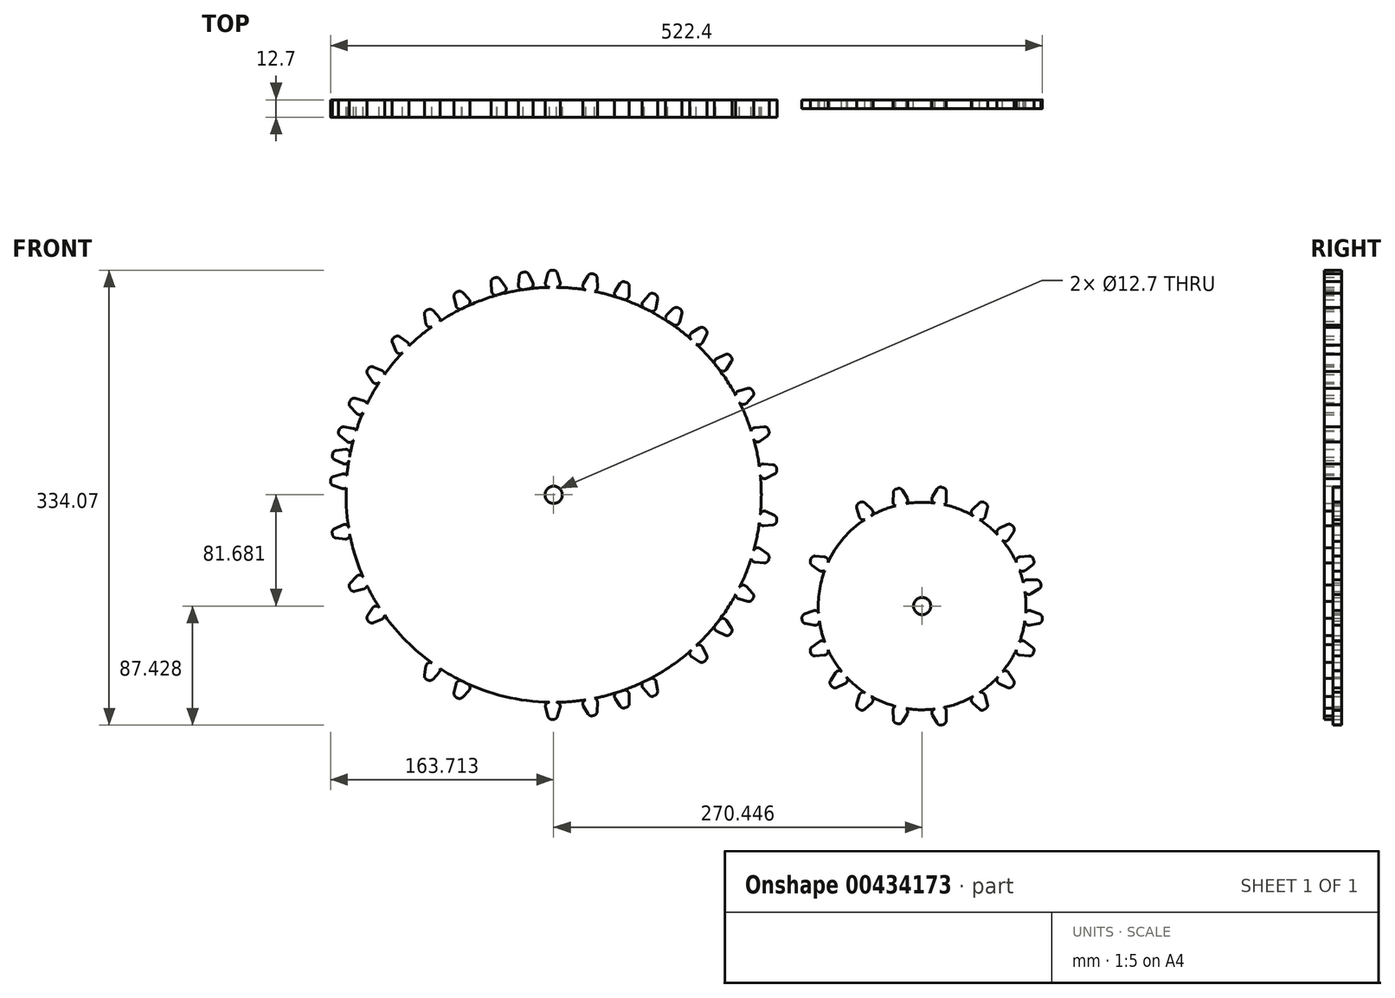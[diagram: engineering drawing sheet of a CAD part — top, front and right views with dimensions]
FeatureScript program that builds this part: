
annotation { "Feature Type Name" : "Feature", "Feature Type Description" : "" }
export const myFeature = defineFeature(function(context is Context, id is Id, definition is map)
    precondition{}
    {
        {
            var Q0;
            Q0=qCreatedBy(makeId("Front.planeOp"),FACE);
            var sketch = newSketch(context, id + "F0", { "sketchPlane" : qUnion([Q0])});
            skCircle(sketch, "E0", {"center": v(-67.8, 42.77) * mm, "radius": 152.4 * mm});
            skCircle(sketch, "E1", {"center": v(227.03, 42.77) * mm, "radius": 76.2 * mm});
            skCircle(sketch, "E2", {"center": v(-67.8, 42.77) * mm, "radius": 6.35 * mm});
            skCircle(sketch, "E3", {"center": v(227.03, 42.77) * mm, "radius": 6.35 * mm});
            skPoint(sketch, "E4.MirrorP", {"position": v(-81.74, -109.18) * mm});
            skLineSegment(sketch, "E5", {"start": v(-69.07, 207.73) * mm, "end": v(-67.96, 207.73) * mm});
            skLineSegment(sketch, "E6", {"start": v(-65.03, 205.55) * mm, "end": v(-63.1, 199.05) * mm});
            skLineSegment(sketch, "E7", {"start": v(-72, 205.48) * mm, "end": v(-73.77, 198.99) * mm});
            skLineSegment(sketch, "E8", {"start": v(-70.83, 195.14) * mm, "end": v(-66.03, 195.14) * mm});
            skArc(sketch, "E9.filletArc", {"start": v(-65.03, 205.55) * mm, "mid": v(-66.13, 207.13) * mm, "end": v(-67.96, 207.73) * mm});
            skArc(sketch, "E10.filletArc", {"start": v(-69.07, 207.73) * mm, "mid": v(-70.92, 207.1) * mm, "end": v(-72, 205.48) * mm});
            skArc(sketch, "E11.filletArc", {"start": v(-66.03, 195.14) * mm, "mid": v(-63.59, 196.36) * mm, "end": v(-63.1, 199.05) * mm});
            skArc(sketch, "E12.filletArc", {"start": v(-73.77, 198.99) * mm, "mid": v(-73.26, 196.34) * mm, "end": v(-70.83, 195.14) * mm});
            skLineSegment(sketch, "E13", {"start": v(-39.2, 205.03) * mm, "end": v(-38.14, 204.74) * mm});
            skLineSegment(sketch, "E14", {"start": v(-35.88, 201.88) * mm, "end": v(-35.7, 195.1) * mm});
            skLineSegment(sketch, "E15", {"start": v(-42.63, 203.62) * mm, "end": v(-46.02, 197.8) * mm});
            skLineSegment(sketch, "E16", {"start": v(-44.17, 193.33) * mm, "end": v(-39.53, 192.08) * mm});
            skArc(sketch, "E17.filletArc", {"start": v(-35.88, 201.88) * mm, "mid": v(-36.53, 203.69) * mm, "end": v(-38.14, 204.74) * mm});
            skArc(sketch, "E18.filletArc", {"start": v(-39.2, 205.03) * mm, "mid": v(-41.16, 204.9) * mm, "end": v(-42.63, 203.62) * mm});
            skArc(sketch, "E19.filletArc", {"start": v(-39.53, 192.08) * mm, "mid": v(-36.86, 192.63) * mm, "end": v(-35.7, 195.1) * mm});
            skArc(sketch, "E20.filletArc", {"start": v(-46.02, 197.8) * mm, "mid": v(-46.2, 195.1) * mm, "end": v(-44.17, 193.33) * mm});
            skLineSegment(sketch, "E21", {"start": v(-111.8, 201.9) * mm, "end": v(-110.75, 202.27) * mm});
            skLineSegment(sketch, "E22", {"start": v(-107.26, 201.22) * mm, "end": v(-103.23, 195.78) * mm});
            skLineSegment(sketch, "E23", {"start": v(-113.8, 198.77) * mm, "end": v(-113.23, 192.07) * mm});
            skLineSegment(sketch, "E24", {"start": v(-109.15, 189.45) * mm, "end": v(-104.64, 191.1) * mm});
            skArc(sketch, "E25.filletArc", {"start": v(-107.26, 201.22) * mm, "mid": v(-108.83, 202.33) * mm, "end": v(-110.75, 202.27) * mm});
            skArc(sketch, "E26.filletArc", {"start": v(-111.8, 201.9) * mm, "mid": v(-113.32, 200.67) * mm, "end": v(-113.8, 198.77) * mm});
            skArc(sketch, "E27.filletArc", {"start": v(-104.64, 191.1) * mm, "mid": v(-102.76, 193.08) * mm, "end": v(-103.23, 195.78) * mm});
            skArc(sketch, "E28.filletArc", {"start": v(-113.23, 192.07) * mm, "mid": v(-111.84, 189.75) * mm, "end": v(-109.15, 189.45) * mm});
            skLineSegment(sketch, "E29", {"start": v(-15.51, 199.28) * mm, "end": v(-14.46, 198.94) * mm});
            skLineSegment(sketch, "E30", {"start": v(-12.33, 195.98) * mm, "end": v(-12.45, 189.2) * mm});
            skLineSegment(sketch, "E31", {"start": v(-19, 198.02) * mm, "end": v(-22.64, 192.36) * mm});
            skLineSegment(sketch, "E32", {"start": v(-21, 187.8) * mm, "end": v(-16.42, 186.35) * mm});
            skArc(sketch, "E33.filletArc", {"start": v(-12.33, 195.98) * mm, "mid": v(-12.9, 197.81) * mm, "end": v(-14.46, 198.94) * mm});
            skArc(sketch, "E34.filletArc", {"start": v(-15.51, 199.28) * mm, "mid": v(-17.47, 199.24) * mm, "end": v(-19, 198.02) * mm});
            skArc(sketch, "E35.filletArc", {"start": v(-16.42, 186.35) * mm, "mid": v(-13.72, 186.78) * mm, "end": v(-12.45, 189.2) * mm});
            skArc(sketch, "E36.filletArc", {"start": v(-22.64, 192.36) * mm, "mid": v(-22.95, 189.68) * mm, "end": v(-21, 187.8) * mm});
            skLineSegment(sketch, "E37", {"start": v(-139.27, 191.52) * mm, "end": v(-138.28, 192.02) * mm});
            skLineSegment(sketch, "E38", {"start": v(-134.69, 191.4) * mm, "end": v(-130.02, 186.5) * mm});
            skLineSegment(sketch, "E39", {"start": v(-140.87, 188.18) * mm, "end": v(-139.49, 181.59) * mm});
            skLineSegment(sketch, "E40", {"start": v(-135.12, 179.5) * mm, "end": v(-130.84, 181.68) * mm});
            skArc(sketch, "E41.filletArc", {"start": v(-134.69, 191.4) * mm, "mid": v(-136.38, 192.31) * mm, "end": v(-138.28, 192.02) * mm});
            skArc(sketch, "E42.filletArc", {"start": v(-139.27, 191.52) * mm, "mid": v(-140.64, 190.12) * mm, "end": v(-140.87, 188.18) * mm});
            skArc(sketch, "E43.filletArc", {"start": v(-130.84, 181.68) * mm, "mid": v(-129.22, 183.88) * mm, "end": v(-130.02, 186.5) * mm});
            skArc(sketch, "E44.filletArc", {"start": v(-139.49, 181.59) * mm, "mid": v(-137.82, 179.46) * mm, "end": v(-135.12, 179.5) * mm});
            skLineSegment(sketch, "E45", {"start": v(5.65, 190.54) * mm, "end": v(6.66, 190.07) * mm});
            skLineSegment(sketch, "E46", {"start": v(8.39, 186.86) * mm, "end": v(7.39, 180.16) * mm});
            skLineSegment(sketch, "E47", {"start": v(2.04, 189.75) * mm, "end": v(-2.3, 184.6) * mm});
            skLineSegment(sketch, "E48", {"start": v(-1.27, 179.88) * mm, "end": v(3.08, 177.85) * mm});
            skArc(sketch, "E49.filletArc", {"start": v(8.39, 186.86) * mm, "mid": v(8.06, 188.75) * mm, "end": v(6.66, 190.07) * mm});
            skArc(sketch, "E50.filletArc", {"start": v(5.65, 190.54) * mm, "mid": v(3.71, 190.76) * mm, "end": v(2.04, 189.75) * mm});
            skArc(sketch, "E51.filletArc", {"start": v(3.08, 177.85) * mm, "mid": v(5.82, 177.93) * mm, "end": v(7.39, 180.16) * mm});
            skArc(sketch, "E52.filletArc", {"start": v(-2.3, 184.6) * mm, "mid": v(-2.96, 181.99) * mm, "end": v(-1.27, 179.88) * mm});
            skLineSegment(sketch, "E53", {"start": v(-90.54, 206.24) * mm, "end": v(-89.44, 206.43) * mm});
            skLineSegment(sketch, "E54", {"start": v(-86.19, 204.8) * mm, "end": v(-83.16, 198.73) * mm});
            skLineSegment(sketch, "E55", {"start": v(-93.04, 203.52) * mm, "end": v(-93.65, 196.81) * mm});
            skLineSegment(sketch, "E56", {"start": v(-90.09, 193.53) * mm, "end": v(-85.36, 194.37) * mm});
            skArc(sketch, "E57.filletArc", {"start": v(-86.19, 204.8) * mm, "mid": v(-87.54, 206.15) * mm, "end": v(-89.44, 206.43) * mm});
            skArc(sketch, "E58.filletArc", {"start": v(-90.54, 206.24) * mm, "mid": v(-92.25, 205.3) * mm, "end": v(-93.04, 203.52) * mm});
            skArc(sketch, "E59.filletArc", {"start": v(-85.36, 194.37) * mm, "mid": v(-83.17, 196) * mm, "end": v(-83.16, 198.73) * mm});
            skArc(sketch, "E60.filletArc", {"start": v(-93.65, 196.81) * mm, "mid": v(-92.68, 194.3) * mm, "end": v(-90.09, 193.53) * mm});
            skLineSegment(sketch, "E61", {"start": v(23.77, 180.12) * mm, "end": v(24.73, 179.56) * mm});
            skLineSegment(sketch, "E62", {"start": v(26.17, 176.21) * mm, "end": v(24.59, 169.62) * mm});
            skLineSegment(sketch, "E63", {"start": v(20.1, 179.64) * mm, "end": v(15.32, 174.9) * mm});
            skLineSegment(sketch, "E64", {"start": v(15.94, 170.1) * mm, "end": v(20.1, 167.7) * mm});
            skArc(sketch, "E65.filletArc", {"start": v(26.17, 176.21) * mm, "mid": v(26, 178.13) * mm, "end": v(24.73, 179.56) * mm});
            skArc(sketch, "E66.filletArc", {"start": v(23.77, 180.12) * mm, "mid": v(21.85, 180.5) * mm, "end": v(20.1, 179.64) * mm});
            skArc(sketch, "E67.filletArc", {"start": v(20.1, 167.7) * mm, "mid": v(22.83, 167.53) * mm, "end": v(24.59, 169.62) * mm});
            skArc(sketch, "E68.filletArc", {"start": v(15.32, 174.9) * mm, "mid": v(14.44, 172.34) * mm, "end": v(15.94, 170.1) * mm});
            skLineSegment(sketch, "E69", {"start": v(-160.9, 178.37) * mm, "end": v(-159.9, 178.84) * mm});
            skLineSegment(sketch, "E70", {"start": v(-156.33, 178.1) * mm, "end": v(-151.84, 173.02) * mm});
            skLineSegment(sketch, "E71", {"start": v(-162.62, 175.09) * mm, "end": v(-161.48, 168.45) * mm});
            skLineSegment(sketch, "E72", {"start": v(-157.19, 166.2) * mm, "end": v(-152.83, 168.24) * mm});
            skArc(sketch, "E73.filletArc", {"start": v(-156.33, 178.1) * mm, "mid": v(-158, 179.06) * mm, "end": v(-159.9, 178.84) * mm});
            skArc(sketch, "E74.filletArc", {"start": v(-160.9, 178.37) * mm, "mid": v(-162.32, 177.02) * mm, "end": v(-162.62, 175.09) * mm});
            skArc(sketch, "E75.filletArc", {"start": v(-152.83, 168.24) * mm, "mid": v(-151.14, 170.38) * mm, "end": v(-151.84, 173.02) * mm});
            skArc(sketch, "E76.filletArc", {"start": v(-161.48, 168.45) * mm, "mid": v(-159.89, 166.27) * mm, "end": v(-157.19, 166.2) * mm});
            skLineSegment(sketch, "E77", {"start": v(42.93, 165.04) * mm, "end": v(43.75, 164.28) * mm});
            skLineSegment(sketch, "E78", {"start": v(44.41, 160.7) * mm, "end": v(41.41, 154.62) * mm});
            skLineSegment(sketch, "E79", {"start": v(39.25, 165.38) * mm, "end": v(33.54, 161.81) * mm});
            skLineSegment(sketch, "E80", {"start": v(33.08, 157) * mm, "end": v(36.61, 153.73) * mm});
            skArc(sketch, "E81.filletArc", {"start": v(44.41, 160.7) * mm, "mid": v(44.67, 162.6) * mm, "end": v(43.75, 164.28) * mm});
            skArc(sketch, "E82.filletArc", {"start": v(42.93, 165.04) * mm, "mid": v(41.15, 165.83) * mm, "end": v(39.25, 165.38) * mm});
            skArc(sketch, "E83.filletArc", {"start": v(36.61, 153.73) * mm, "mid": v(39.24, 152.97) * mm, "end": v(41.41, 154.62) * mm});
            skArc(sketch, "E84.filletArc", {"start": v(33.54, 161.81) * mm, "mid": v(32.12, 159.52) * mm, "end": v(33.08, 157) * mm});
            skLineSegment(sketch, "E85", {"start": v(-185.24, 158.1) * mm, "end": v(-184.37, 158.79) * mm});
            skLineSegment(sketch, "E86", {"start": v(-180.72, 158.86) * mm, "end": v(-175.22, 154.9) * mm});
            skLineSegment(sketch, "E87", {"start": v(-186.19, 154.53) * mm, "end": v(-183.6, 148.31) * mm});
            skLineSegment(sketch, "E88", {"start": v(-178.92, 147.08) * mm, "end": v(-175.13, 150.02) * mm});
            skArc(sketch, "E89.filletArc", {"start": v(-180.72, 158.86) * mm, "mid": v(-182.55, 159.43) * mm, "end": v(-184.37, 158.79) * mm});
            skArc(sketch, "E90.filletArc", {"start": v(-185.24, 158.1) * mm, "mid": v(-186.32, 156.48) * mm, "end": v(-186.19, 154.53) * mm});
            skArc(sketch, "E91.filletArc", {"start": v(-175.13, 150.02) * mm, "mid": v(-173.95, 152.48) * mm, "end": v(-175.22, 154.9) * mm});
            skArc(sketch, "E92.filletArc", {"start": v(-183.6, 148.31) * mm, "mid": v(-181.57, 146.54) * mm, "end": v(-178.92, 147.08) * mm});
            skLineSegment(sketch, "E93", {"start": v(61.71, 145.04) * mm, "end": v(62.43, 144.2) * mm});
            skLineSegment(sketch, "E94", {"start": v(62.63, 140.55) * mm, "end": v(58.9, 134.9) * mm});
            skLineSegment(sketch, "E95", {"start": v(58.1, 145.85) * mm, "end": v(51.99, 143.03) * mm});
            skLineSegment(sketch, "E96", {"start": v(50.93, 138.3) * mm, "end": v(54.02, 134.62) * mm});
            skArc(sketch, "E97.filletArc", {"start": v(62.63, 140.55) * mm, "mid": v(63.14, 142.4) * mm, "end": v(62.43, 144.2) * mm});
            skArc(sketch, "E98.filletArc", {"start": v(61.71, 145.04) * mm, "mid": v(60.04, 146.06) * mm, "end": v(58.1, 145.85) * mm});
            skArc(sketch, "E99.filletArc", {"start": v(54.02, 134.62) * mm, "mid": v(56.53, 133.54) * mm, "end": v(58.9, 134.9) * mm});
            skArc(sketch, "E100.filletArc", {"start": v(51.99, 143.03) * mm, "mid": v(50.3, 140.93) * mm, "end": v(50.93, 138.3) * mm});
            skLineSegment(sketch, "E101", {"start": v(-204.16, 135.08) * mm, "end": v(-203.44, 135.92) * mm});
            skLineSegment(sketch, "E102", {"start": v(-199.88, 136.7) * mm, "end": v(-193.7, 133.92) * mm});
            skLineSegment(sketch, "E103", {"start": v(-204.38, 131.39) * mm, "end": v(-200.62, 125.8) * mm});
            skLineSegment(sketch, "E104", {"start": v(-195.79, 125.51) * mm, "end": v(-192.65, 129.15) * mm});
            skArc(sketch, "E105.filletArc", {"start": v(-199.88, 136.7) * mm, "mid": v(-201.79, 136.9) * mm, "end": v(-203.44, 135.92) * mm});
            skArc(sketch, "E106.filletArc", {"start": v(-204.16, 135.08) * mm, "mid": v(-204.9, 133.27) * mm, "end": v(-204.38, 131.39) * mm});
            skArc(sketch, "E107.filletArc", {"start": v(-192.65, 129.15) * mm, "mid": v(-191.98, 131.8) * mm, "end": v(-193.7, 133.92) * mm});
            skArc(sketch, "E108.filletArc", {"start": v(-200.62, 125.8) * mm, "mid": v(-198.28, 124.46) * mm, "end": v(-195.79, 125.51) * mm});
            skLineSegment(sketch, "E109", {"start": v(-217.46, 111.31) * mm, "end": v(-216.87, 112.25) * mm});
            skLineSegment(sketch, "E110", {"start": v(-213.47, 113.56) * mm, "end": v(-206.95, 111.72) * mm});
            skLineSegment(sketch, "E111", {"start": v(-217.13, 107.62) * mm, "end": v(-212.58, 102.66) * mm});
            skLineSegment(sketch, "E112", {"start": v(-207.76, 103.1) * mm, "end": v(-205.2, 107.16) * mm});
            skArc(sketch, "E113.filletArc", {"start": v(-213.47, 113.56) * mm, "mid": v(-215.39, 113.47) * mm, "end": v(-216.87, 112.25) * mm});
            skArc(sketch, "E114.filletArc", {"start": v(-217.46, 111.31) * mm, "mid": v(-217.92, 109.41) * mm, "end": v(-217.13, 107.62) * mm});
            skArc(sketch, "E115.filletArc", {"start": v(-205.2, 107.16) * mm, "mid": v(-204.93, 109.88) * mm, "end": v(-206.95, 111.72) * mm});
            skArc(sketch, "E116.filletArc", {"start": v(-212.58, 102.66) * mm, "mid": v(-210.07, 101.69) * mm, "end": v(-207.76, 103.1) * mm});
            skLineSegment(sketch, "E117", {"start": v(78.04, 119.55) * mm, "end": v(78.6, 118.59) * mm});
            skLineSegment(sketch, "E118", {"start": v(78.17, 114.97) * mm, "end": v(73.5, 110.05) * mm});
            skLineSegment(sketch, "E119", {"start": v(74.62, 120.97) * mm, "end": v(68.11, 119.25) * mm});
            skLineSegment(sketch, "E120", {"start": v(66.25, 114.78) * mm, "end": v(68.65, 110.62) * mm});
            skArc(sketch, "E121.filletArc", {"start": v(78.17, 114.97) * mm, "mid": v(78.98, 116.7) * mm, "end": v(78.6, 118.59) * mm});
            skArc(sketch, "E122.filletArc", {"start": v(78.04, 119.55) * mm, "mid": v(76.57, 120.84) * mm, "end": v(74.62, 120.97) * mm});
            skArc(sketch, "E123.filletArc", {"start": v(68.65, 110.62) * mm, "mid": v(70.94, 109.12) * mm, "end": v(73.5, 110.05) * mm});
            skArc(sketch, "E124.filletArc", {"start": v(68.11, 119.25) * mm, "mid": v(66.08, 117.48) * mm, "end": v(66.25, 114.78) * mm});
            skLineSegment(sketch, "E125", {"start": v(-225.47, 89.9) * mm, "end": v(-225, 90.9) * mm});
            skLineSegment(sketch, "E126", {"start": v(-221.8, 92.63) * mm, "end": v(-215.1, 91.63) * mm});
            skLineSegment(sketch, "E127", {"start": v(-224.68, 86.29) * mm, "end": v(-219.54, 81.94) * mm});
            skLineSegment(sketch, "E128", {"start": v(-214.8, 82.98) * mm, "end": v(-212.78, 87.33) * mm});
            skArc(sketch, "E129.filletArc", {"start": v(-221.8, 92.63) * mm, "mid": v(-223.68, 92.3) * mm, "end": v(-225, 90.9) * mm});
            skArc(sketch, "E130.filletArc", {"start": v(-225.47, 89.9) * mm, "mid": v(-225.69, 87.96) * mm, "end": v(-224.68, 86.29) * mm});
            skArc(sketch, "E131.filletArc", {"start": v(-212.78, 87.33) * mm, "mid": v(-212.86, 90.06) * mm, "end": v(-215.1, 91.63) * mm});
            skArc(sketch, "E132.filletArc", {"start": v(-219.54, 81.94) * mm, "mid": v(-216.92, 81.29) * mm, "end": v(-214.8, 82.98) * mm});
            skLineSegment(sketch, "E133", {"start": v(89.81, 90.77) * mm, "end": v(90.2, 89.73) * mm});
            skLineSegment(sketch, "E134", {"start": v(89.14, 86.24) * mm, "end": v(83.7, 82.2) * mm});
            skLineSegment(sketch, "E135", {"start": v(86.7, 92.77) * mm, "end": v(79.99, 92.2) * mm});
            skLineSegment(sketch, "E136", {"start": v(77.37, 88.13) * mm, "end": v(79.02, 83.61) * mm});
            skArc(sketch, "E137.filletArc", {"start": v(89.14, 86.24) * mm, "mid": v(90.25, 87.81) * mm, "end": v(90.2, 89.73) * mm});
            skArc(sketch, "E138.filletArc", {"start": v(89.81, 90.77) * mm, "mid": v(88.6, 92.3) * mm, "end": v(86.7, 92.77) * mm});
            skArc(sketch, "E139.filletArc", {"start": v(79.02, 83.61) * mm, "mid": v(81, 81.74) * mm, "end": v(83.7, 82.2) * mm});
            skArc(sketch, "E140.filletArc", {"start": v(79.99, 92.2) * mm, "mid": v(77.67, 90.81) * mm, "end": v(77.37, 88.13) * mm});
            skLineSegment(sketch, "E141", {"start": v(-230.22, 71.8) * mm, "end": v(-230.03, 72.89) * mm});
            skLineSegment(sketch, "E142", {"start": v(-227.37, 75.39) * mm, "end": v(-220.64, 76.16) * mm});
            skLineSegment(sketch, "E143", {"start": v(-228.52, 68.51) * mm, "end": v(-222.43, 65.64) * mm});
            skLineSegment(sketch, "E144", {"start": v(-218.13, 67.87) * mm, "end": v(-217.3, 72.6) * mm});
            skArc(sketch, "E145.filletArc", {"start": v(-227.37, 75.39) * mm, "mid": v(-229.11, 74.58) * mm, "end": v(-230.03, 72.89) * mm});
            skArc(sketch, "E146.filletArc", {"start": v(-230.22, 71.8) * mm, "mid": v(-229.92, 69.87) * mm, "end": v(-228.52, 68.51) * mm});
            skArc(sketch, "E147.filletArc", {"start": v(-217.3, 72.6) * mm, "mid": v(-218.07, 75.22) * mm, "end": v(-220.64, 76.16) * mm});
            skArc(sketch, "E148.filletArc", {"start": v(-222.43, 65.64) * mm, "mid": v(-219.73, 65.7) * mm, "end": v(-218.13, 67.87) * mm});
            skLineSegment(sketch, "E149", {"start": v(95.78, 62.35) * mm, "end": v(95.98, 61.26) * mm});
            skLineSegment(sketch, "E150", {"start": v(94.34, 58) * mm, "end": v(88.27, 54.98) * mm});
            skLineSegment(sketch, "E151", {"start": v(93.06, 64.86) * mm, "end": v(86.36, 65.47) * mm});
            skLineSegment(sketch, "E152", {"start": v(83.08, 61.9) * mm, "end": v(83.91, 57.17) * mm});
            skArc(sketch, "E153.filletArc", {"start": v(94.34, 58) * mm, "mid": v(95.7, 59.36) * mm, "end": v(95.98, 61.26) * mm});
            skArc(sketch, "E154.filletArc", {"start": v(95.78, 62.35) * mm, "mid": v(94.85, 64.06) * mm, "end": v(93.06, 64.86) * mm});
            skArc(sketch, "E155.filletArc", {"start": v(83.91, 57.17) * mm, "mid": v(85.54, 54.98) * mm, "end": v(88.27, 54.98) * mm});
            skArc(sketch, "E156.filletArc", {"start": v(86.36, 65.47) * mm, "mid": v(83.83, 64.5) * mm, "end": v(83.08, 61.9) * mm});
            skLineSegment(sketch, "E157", {"start": v(-231.52, 52.48) * mm, "end": v(-231.47, 53.58) * mm});
            skLineSegment(sketch, "E158", {"start": v(-229.15, 56.4) * mm, "end": v(-222.56, 58) * mm});
            skLineSegment(sketch, "E159", {"start": v(-229.42, 49.43) * mm, "end": v(-223.01, 47.35) * mm});
            skLineSegment(sketch, "E160", {"start": v(-219.03, 50.1) * mm, "end": v(-218.8, 54.9) * mm});
            skArc(sketch, "E161.filletArc", {"start": v(-229.15, 56.4) * mm, "mid": v(-230.77, 55.38) * mm, "end": v(-231.47, 53.58) * mm});
            skArc(sketch, "E162.filletArc", {"start": v(-231.52, 52.48) * mm, "mid": v(-230.98, 50.6) * mm, "end": v(-229.42, 49.43) * mm});
            skArc(sketch, "E163.filletArc", {"start": v(-218.8, 54.9) * mm, "mid": v(-219.9, 57.4) * mm, "end": v(-222.56, 58) * mm});
            skArc(sketch, "E164.filletArc", {"start": v(-223.01, 47.35) * mm, "mid": v(-220.34, 47.74) * mm, "end": v(-219.03, 50.1) * mm});
            skLineSegment(sketch, "E165.MirrorCS", {"start": v(-69.07, -122.2) * mm, "end": v(-67.96, -122.2) * mm});
            skLineSegment(sketch, "E166.MirrorCS", {"start": v(-230.37, 14.67) * mm, "end": v(-230.18, 13.58) * mm});
            skLineSegment(sketch, "E167.MirrorCS", {"start": v(89.81, -5.23) * mm, "end": v(90.2, -4.2) * mm});
            skLineSegment(sketch, "E168.MirrorCS", {"start": v(95.78, 23.19) * mm, "end": v(95.98, 24.28) * mm});
            skArc(sketch, "E169.MirrorCS", {"start": v(89.81, -5.23) * mm, "mid": v(88.6, -6.76) * mm, "end": v(86.7, -7.23) * mm});
            skArc(sketch, "E170.MirrorCS", {"start": v(95.78, 23.19) * mm, "mid": v(94.85, 21.47) * mm, "end": v(93.06, 20.68) * mm});
            skArc(sketch, "E171.MirrorCS", {"start": v(-230.37, 14.67) * mm, "mid": v(-230.07, 16.6) * mm, "end": v(-228.67, 17.96) * mm});
            skArc(sketch, "E172.MirrorCS", {"start": v(89.14, -0.7) * mm, "mid": v(90.25, -2.27) * mm, "end": v(90.2, -4.2) * mm});
            skArc(sketch, "E173.MirrorCS", {"start": v(94.34, 27.54) * mm, "mid": v(95.7, 26.18) * mm, "end": v(95.98, 24.28) * mm});
            skArc(sketch, "E174.MirrorCS", {"start": v(-227.52, 11.08) * mm, "mid": v(-229.26, 11.89) * mm, "end": v(-230.18, 13.58) * mm});
            skLineSegment(sketch, "E175.MirrorCS", {"start": v(-39.2, -119.5) * mm, "end": v(-38.14, -119.2) * mm});
            skArc(sketch, "E176.MirrorCS", {"start": v(-69.07, -122.2) * mm, "mid": v(-70.92, -121.57) * mm, "end": v(-72, -119.94) * mm});
            skArc(sketch, "E177.MirrorCS", {"start": v(-65.03, -120.01) * mm, "mid": v(-66.13, -121.59) * mm, "end": v(-67.96, -122.2) * mm});
            skLineSegment(sketch, "E178.MirrorCS", {"start": v(61.71, -59.5) * mm, "end": v(62.43, -58.66) * mm});
            skLineSegment(sketch, "E179.MirrorCS", {"start": v(-15.51, -113.74) * mm, "end": v(-14.46, -113.4) * mm});
            skLineSegment(sketch, "E180.MirrorCS", {"start": v(-160.9, -92.83) * mm, "end": v(-159.9, -93.3) * mm});
            skArc(sketch, "E181.MirrorCS", {"start": v(-218.88, 31.87) * mm, "mid": v(-219.76, 29.29) * mm, "end": v(-222.36, 28.45) * mm});
            skArc(sketch, "E182.MirrorCS", {"start": v(-160.9, -92.83) * mm, "mid": v(-162.32, -91.48) * mm, "end": v(-162.62, -89.55) * mm});
            skArc(sketch, "E183.MirrorCS", {"start": v(61.71, -59.5) * mm, "mid": v(60.04, -60.52) * mm, "end": v(58.1, -60.31) * mm});
            skArc(sketch, "E184.MirrorCS", {"start": v(-15.51, -113.74) * mm, "mid": v(-17.47, -113.7) * mm, "end": v(-19, -112.48) * mm});
            skArc(sketch, "E185.MirrorCS", {"start": v(-39.2, -119.5) * mm, "mid": v(-41.16, -119.37) * mm, "end": v(-42.63, -118.08) * mm});
            skArc(sketch, "E186.MirrorCS", {"start": v(-156.33, -92.55) * mm, "mid": v(-158, -93.52) * mm, "end": v(-159.9, -93.3) * mm});
            skArc(sketch, "E187.MirrorCS", {"start": v(-231.77, 33.17) * mm, "mid": v(-231.4, 35.1) * mm, "end": v(-229.94, 36.4) * mm});
            skArc(sketch, "E188.MirrorCS", {"start": v(-12.33, -110.44) * mm, "mid": v(-12.9, -112.27) * mm, "end": v(-14.46, -113.4) * mm});
            skArc(sketch, "E189.MirrorCS", {"start": v(-35.88, -116.34) * mm, "mid": v(-36.53, -118.15) * mm, "end": v(-38.14, -119.2) * mm});
            skArc(sketch, "E190.MirrorCS", {"start": v(-229.06, 29.48) * mm, "mid": v(-230.77, 30.35) * mm, "end": v(-231.62, 32.08) * mm});
            skArc(sketch, "E191.MirrorCS", {"start": v(62.63, -55.01) * mm, "mid": v(63.14, -56.87) * mm, "end": v(62.43, -58.66) * mm});
            skLineSegment(sketch, "E192.MirrorCS", {"start": v(-231.77, 33.17) * mm, "end": v(-231.62, 32.08) * mm});
            skLineSegment(sketch, "E193.MirrorCS", {"start": v(42.93, -79.5) * mm, "end": v(43.75, -78.74) * mm});
            skLineSegment(sketch, "E194.MirrorCS", {"start": v(-217.46, -25.77) * mm, "end": v(-216.87, -26.7) * mm});
            skLineSegment(sketch, "E195.MirrorCS", {"start": v(5.65, -105) * mm, "end": v(6.66, -104.53) * mm});
            skLineSegment(sketch, "E196.MirrorCS", {"start": v(-229.06, 29.48) * mm, "end": v(-222.36, 28.45) * mm});
            skLineSegment(sketch, "E197.MirrorCS", {"start": v(-204.16, -49.54) * mm, "end": v(-203.44, -50.38) * mm});
            skLineSegment(sketch, "E198.MirrorCS", {"start": v(78.04, -34) * mm, "end": v(78.6, -33.05) * mm});
            skLineSegment(sketch, "E199.MirrorCS", {"start": v(-139.27, -105.98) * mm, "end": v(-138.28, -106.48) * mm});
            skArc(sketch, "E200.MirrorCS", {"start": v(-205.2, -21.62) * mm, "mid": v(-204.93, -24.34) * mm, "end": v(-206.95, -26.18) * mm});
            skArc(sketch, "E201.MirrorCS", {"start": v(-212.78, -1.8) * mm, "mid": v(-212.86, -4.52) * mm, "end": v(-215.1, -6.1) * mm});
            skArc(sketch, "E202.MirrorCS", {"start": v(-217.44, 13.87) * mm, "mid": v(-218.22, 11.25) * mm, "end": v(-220.79, 10.3) * mm});
            skArc(sketch, "E203.MirrorCS", {"start": v(-16.42, -100.81) * mm, "mid": v(-13.72, -101.24) * mm, "end": v(-12.45, -103.66) * mm});
            skArc(sketch, "E204.MirrorCS", {"start": v(-185.24, -72.57) * mm, "mid": v(-186.32, -70.94) * mm, "end": v(-186.19, -68.99) * mm});
            skArc(sketch, "E205.MirrorCS", {"start": v(-204.16, -49.54) * mm, "mid": v(-204.9, -47.73) * mm, "end": v(-204.38, -45.85) * mm});
            skArc(sketch, "E206.MirrorCS", {"start": v(78.04, -34) * mm, "mid": v(76.57, -35.3) * mm, "end": v(74.62, -35.43) * mm});
            skArc(sketch, "E207.MirrorCS", {"start": v(-111.8, -116.35) * mm, "mid": v(-113.32, -115.13) * mm, "end": v(-113.8, -113.23) * mm});
            skArc(sketch, "E208.MirrorCS", {"start": v(-139.27, -105.98) * mm, "mid": v(-140.64, -104.58) * mm, "end": v(-140.87, -102.64) * mm});
            skArc(sketch, "E209.MirrorCS", {"start": v(-90.54, -120.7) * mm, "mid": v(-92.25, -119.76) * mm, "end": v(-93.04, -117.98) * mm});
            skArc(sketch, "E210.MirrorCS", {"start": v(-217.46, -25.77) * mm, "mid": v(-217.92, -23.87) * mm, "end": v(-217.13, -22.08) * mm});
            skArc(sketch, "E211.MirrorCS", {"start": v(-225.47, -4.36) * mm, "mid": v(-225.69, -2.42) * mm, "end": v(-224.68, -0.75) * mm});
            skArc(sketch, "E212.MirrorCS", {"start": v(23.77, -94.58) * mm, "mid": v(21.85, -94.96) * mm, "end": v(20.1, -94.1) * mm});
            skArc(sketch, "E213.MirrorCS", {"start": v(42.93, -79.5) * mm, "mid": v(41.15, -80.3) * mm, "end": v(39.25, -79.84) * mm});
            skArc(sketch, "E214.MirrorCS", {"start": v(-199.88, -51.17) * mm, "mid": v(-201.79, -51.37) * mm, "end": v(-203.44, -50.38) * mm});
            skArc(sketch, "E215.MirrorCS", {"start": v(78.17, -29.43) * mm, "mid": v(78.98, -31.17) * mm, "end": v(78.6, -33.05) * mm});
            skArc(sketch, "E216.MirrorCS", {"start": v(-134.69, -105.87) * mm, "mid": v(-136.38, -106.77) * mm, "end": v(-138.28, -106.48) * mm});
            skArc(sketch, "E217.MirrorCS", {"start": v(-86.19, -119.25) * mm, "mid": v(-87.54, -120.61) * mm, "end": v(-89.44, -120.9) * mm});
            skArc(sketch, "E218.MirrorCS", {"start": v(8.39, -101.32) * mm, "mid": v(8.06, -103.22) * mm, "end": v(6.66, -104.53) * mm});
            skArc(sketch, "E219.MirrorCS", {"start": v(26.17, -90.67) * mm, "mid": v(26, -92.59) * mm, "end": v(24.73, -94.02) * mm});
            skArc(sketch, "E220.MirrorCS", {"start": v(44.41, -75.16) * mm, "mid": v(44.67, -77.06) * mm, "end": v(43.75, -78.74) * mm});
            skArc(sketch, "E221.MirrorCS", {"start": v(-213.47, -28.02) * mm, "mid": v(-215.39, -27.93) * mm, "end": v(-216.87, -26.7) * mm});
            skArc(sketch, "E222.MirrorCS", {"start": v(-221.8, -7.1) * mm, "mid": v(-223.68, -6.76) * mm, "end": v(-225, -5.37) * mm});
            skArc(sketch, "E223.MirrorCS", {"start": v(-73.77, -113.45) * mm, "mid": v(-73.26, -110.8) * mm, "end": v(-70.83, -109.6) * mm});
            skArc(sketch, "E224.MirrorCS", {"start": v(-66.03, -109.6) * mm, "mid": v(-63.59, -110.82) * mm, "end": v(-63.1, -113.51) * mm});
            skLineSegment(sketch, "E225.MirrorCS", {"start": v(-70.83, -109.6) * mm, "end": v(-66.03, -109.6) * mm});
            skLineSegment(sketch, "E226.MirrorCS", {"start": v(-72, -119.94) * mm, "end": v(-73.77, -113.45) * mm});
            skLineSegment(sketch, "E227.MirrorCS", {"start": v(-65.03, -120.01) * mm, "end": v(-63.1, -113.51) * mm});
            skLineSegment(sketch, "E228.MirrorCS", {"start": v(-214.8, 2.56) * mm, "end": v(-212.78, -1.8) * mm});
            skLineSegment(sketch, "E229.MirrorCS", {"start": v(58.1, -60.31) * mm, "end": v(51.99, -57.5) * mm});
            skLineSegment(sketch, "E230.MirrorCS", {"start": v(-199.88, -51.17) * mm, "end": v(-193.7, -48.38) * mm});
            skLineSegment(sketch, "E231.MirrorCS", {"start": v(-228.67, 17.96) * mm, "end": v(-222.58, 20.83) * mm});
            skLineSegment(sketch, "E232.MirrorCS", {"start": v(20.1, -94.1) * mm, "end": v(15.32, -89.36) * mm});
            skLineSegment(sketch, "E233.MirrorCS", {"start": v(-156.33, -92.55) * mm, "end": v(-151.84, -87.48) * mm});
            skLineSegment(sketch, "E234.MirrorCS", {"start": v(-180.72, -73.32) * mm, "end": v(-175.22, -69.36) * mm});
            skLineSegment(sketch, "E235.MirrorCS", {"start": v(-225.47, -4.36) * mm, "end": v(-225, -5.37) * mm});
            skLineSegment(sketch, "E236.MirrorCS", {"start": v(23.77, -94.58) * mm, "end": v(24.73, -94.02) * mm});
            skLineSegment(sketch, "E237.MirrorCS", {"start": v(-221.8, -7.1) * mm, "end": v(-215.1, -6.1) * mm});
            skLineSegment(sketch, "E238.MirrorCS", {"start": v(-213.47, -28.02) * mm, "end": v(-206.95, -26.18) * mm});
            skLineSegment(sketch, "E239.MirrorCS", {"start": v(-227.52, 11.08) * mm, "end": v(-220.79, 10.3) * mm});
            skLineSegment(sketch, "E240.MirrorCS", {"start": v(-12.33, -110.44) * mm, "end": v(-12.45, -103.66) * mm});
            skLineSegment(sketch, "E241.MirrorCS", {"start": v(8.39, -101.32) * mm, "end": v(7.39, -94.62) * mm});
            skLineSegment(sketch, "E242.MirrorCS", {"start": v(-90.54, -120.7) * mm, "end": v(-89.44, -120.9) * mm});
            skLineSegment(sketch, "E243.MirrorCS", {"start": v(-185.24, -72.57) * mm, "end": v(-184.37, -73.25) * mm});
            skLineSegment(sketch, "E244.MirrorCS", {"start": v(-111.8, -116.35) * mm, "end": v(-110.75, -116.73) * mm});
            skArc(sketch, "E245.MirrorCS", {"start": v(51.99, -57.5) * mm, "mid": v(50.3, -55.39) * mm, "end": v(50.93, -52.77) * mm});
            skArc(sketch, "E246.MirrorCS", {"start": v(-222.58, 20.83) * mm, "mid": v(-219.87, 20.77) * mm, "end": v(-218.28, 18.6) * mm});
            skArc(sketch, "E247.MirrorCS", {"start": v(-2.3, -99.07) * mm, "mid": v(-2.96, -96.45) * mm, "end": v(-1.27, -94.34) * mm});
            skArc(sketch, "E248.MirrorCS", {"start": v(-152.83, -82.7) * mm, "mid": v(-151.14, -84.84) * mm, "end": v(-151.84, -87.48) * mm});
            skArc(sketch, "E249.MirrorCS", {"start": v(-175.13, -64.48) * mm, "mid": v(-173.95, -66.95) * mm, "end": v(-175.22, -69.36) * mm});
            skArc(sketch, "E250.MirrorCS", {"start": v(-192.65, -43.61) * mm, "mid": v(-191.98, -46.26) * mm, "end": v(-193.7, -48.38) * mm});
            skArc(sketch, "E251.MirrorCS", {"start": v(54.02, -49.09) * mm, "mid": v(56.53, -48) * mm, "end": v(58.9, -49.36) * mm});
            skArc(sketch, "E252.MirrorCS", {"start": v(3.08, -92.3) * mm, "mid": v(5.82, -92.39) * mm, "end": v(7.39, -94.62) * mm});
            skArc(sketch, "E253.MirrorCS", {"start": v(20.1, -82.16) * mm, "mid": v(22.83, -82) * mm, "end": v(24.59, -84.08) * mm});
            skArc(sketch, "E254.MirrorCS", {"start": v(36.61, -68.2) * mm, "mid": v(39.24, -67.43) * mm, "end": v(41.41, -69.08) * mm});
            skArc(sketch, "E255.MirrorCS", {"start": v(-39.53, -106.54) * mm, "mid": v(-36.86, -107.1) * mm, "end": v(-35.7, -109.57) * mm});
            skArc(sketch, "E256.MirrorCS", {"start": v(5.65, -105) * mm, "mid": v(3.71, -105.22) * mm, "end": v(2.04, -104.2) * mm});
            skArc(sketch, "E257.MirrorCS", {"start": v(-180.72, -73.32) * mm, "mid": v(-182.55, -73.89) * mm, "end": v(-184.37, -73.25) * mm});
            skArc(sketch, "E258.MirrorCS", {"start": v(-107.26, -115.68) * mm, "mid": v(-108.83, -116.79) * mm, "end": v(-110.75, -116.73) * mm});
            skLineSegment(sketch, "E259.MirrorCS", {"start": v(77.37, -2.59) * mm, "end": v(79.02, 1.93) * mm});
            skLineSegment(sketch, "E260.MirrorCS", {"start": v(83.08, 23.63) * mm, "end": v(83.91, 28.36) * mm});
            skLineSegment(sketch, "E261.MirrorCS", {"start": v(-157.19, -80.67) * mm, "end": v(-152.83, -82.7) * mm});
            skLineSegment(sketch, "E262.MirrorCS", {"start": v(-178.92, -61.54) * mm, "end": v(-175.13, -64.48) * mm});
            skLineSegment(sketch, "E263.MirrorCS", {"start": v(-195.79, -39.97) * mm, "end": v(-192.65, -43.61) * mm});
            skLineSegment(sketch, "E264.MirrorCS", {"start": v(66.25, -29.24) * mm, "end": v(68.65, -25.08) * mm});
            skLineSegment(sketch, "E265.MirrorCS", {"start": v(-109.15, -103.92) * mm, "end": v(-104.64, -105.56) * mm});
            skLineSegment(sketch, "E266.MirrorCS", {"start": v(-135.12, -93.96) * mm, "end": v(-130.84, -96.14) * mm});
            skLineSegment(sketch, "E267.MirrorCS", {"start": v(-90.09, -108) * mm, "end": v(-85.36, -108.83) * mm});
            skLineSegment(sketch, "E268.MirrorCS", {"start": v(-44.17, -107.79) * mm, "end": v(-39.53, -106.54) * mm});
            skLineSegment(sketch, "E269.MirrorCS", {"start": v(-42.63, -118.08) * mm, "end": v(-46.02, -112.27) * mm});
            skLineSegment(sketch, "E270.MirrorCS", {"start": v(-35.88, -116.34) * mm, "end": v(-35.7, -109.57) * mm});
            skLineSegment(sketch, "E271.MirrorCS", {"start": v(-219.53, 36.63) * mm, "end": v(-218.88, 31.87) * mm});
            skLineSegment(sketch, "E272.MirrorCS", {"start": v(-204.38, -45.85) * mm, "end": v(-200.62, -40.26) * mm});
            skLineSegment(sketch, "E273.MirrorCS", {"start": v(50.93, -52.77) * mm, "end": v(54.02, -49.09) * mm});
            skLineSegment(sketch, "E274.MirrorCS", {"start": v(74.62, -35.43) * mm, "end": v(68.11, -33.71) * mm});
            skLineSegment(sketch, "E275.MirrorCS", {"start": v(-207.76, -17.55) * mm, "end": v(-205.2, -21.62) * mm});
            skLineSegment(sketch, "E276.MirrorCS", {"start": v(86.7, -7.23) * mm, "end": v(79.99, -6.67) * mm});
            skLineSegment(sketch, "E277.MirrorCS", {"start": v(93.06, 20.68) * mm, "end": v(86.36, 20.07) * mm});
            skLineSegment(sketch, "E278.MirrorCS", {"start": v(-218.28, 18.6) * mm, "end": v(-217.44, 13.87) * mm});
            skLineSegment(sketch, "E279.MirrorCS", {"start": v(-140.87, -102.64) * mm, "end": v(-139.49, -96.05) * mm});
            skLineSegment(sketch, "E280.MirrorCS", {"start": v(-21, -102.26) * mm, "end": v(-16.42, -100.81) * mm});
            skLineSegment(sketch, "E281.MirrorCS", {"start": v(-93.04, -117.98) * mm, "end": v(-93.65, -111.27) * mm});
            skLineSegment(sketch, "E282.MirrorCS", {"start": v(-1.27, -94.34) * mm, "end": v(3.08, -92.3) * mm});
            skLineSegment(sketch, "E283.MirrorCS", {"start": v(-162.62, -89.55) * mm, "end": v(-161.48, -82.91) * mm});
            skLineSegment(sketch, "E284.MirrorCS", {"start": v(15.94, -84.56) * mm, "end": v(20.1, -82.16) * mm});
            skLineSegment(sketch, "E285.MirrorCS", {"start": v(-186.19, -68.99) * mm, "end": v(-183.6, -62.77) * mm});
            skLineSegment(sketch, "E286.MirrorCS", {"start": v(33.08, -71.45) * mm, "end": v(36.61, -68.2) * mm});
            skLineSegment(sketch, "E287.MirrorCS", {"start": v(-113.8, -113.23) * mm, "end": v(-113.23, -106.53) * mm});
            skLineSegment(sketch, "E288.MirrorCS", {"start": v(-229.94, 36.4) * mm, "end": v(-223.74, 39.03) * mm});
            skLineSegment(sketch, "E289.MirrorCS", {"start": v(-217.13, -22.08) * mm, "end": v(-212.58, -17.12) * mm});
            skLineSegment(sketch, "E290.MirrorCS", {"start": v(-224.68, -0.75) * mm, "end": v(-219.54, 3.6) * mm});
            skLineSegment(sketch, "E291.MirrorCS", {"start": v(78.17, -29.43) * mm, "end": v(73.5, -24.5) * mm});
            skLineSegment(sketch, "E292.MirrorCS", {"start": v(-19, -112.48) * mm, "end": v(-22.64, -106.82) * mm});
            skLineSegment(sketch, "E293.MirrorCS", {"start": v(89.14, -0.7) * mm, "end": v(83.7, 3.33) * mm});
            skLineSegment(sketch, "E294.MirrorCS", {"start": v(2.04, -104.2) * mm, "end": v(-2.3, -99.07) * mm});
            skLineSegment(sketch, "E295.MirrorCS", {"start": v(94.34, 27.54) * mm, "end": v(88.27, 30.56) * mm});
            skLineSegment(sketch, "E296.MirrorCS", {"start": v(-134.69, -105.87) * mm, "end": v(-130.02, -100.96) * mm});
            skLineSegment(sketch, "E297.MirrorCS", {"start": v(-86.19, -119.25) * mm, "end": v(-83.16, -113.19) * mm});
            skLineSegment(sketch, "E298.MirrorCS", {"start": v(39.25, -79.84) * mm, "end": v(33.54, -76.27) * mm});
            skLineSegment(sketch, "E299.MirrorCS", {"start": v(-107.26, -115.68) * mm, "end": v(-103.23, -110.24) * mm});
            skLineSegment(sketch, "E300.MirrorCS", {"start": v(62.63, -55.01) * mm, "end": v(58.9, -49.36) * mm});
            skLineSegment(sketch, "E301.MirrorCS", {"start": v(26.17, -90.67) * mm, "end": v(24.59, -84.08) * mm});
            skLineSegment(sketch, "E302.MirrorCS", {"start": v(44.41, -75.16) * mm, "end": v(41.41, -69.08) * mm});
            skArc(sketch, "E303.MirrorCS", {"start": v(79.99, -6.67) * mm, "mid": v(77.67, -5.27) * mm, "end": v(77.37, -2.59) * mm});
            skArc(sketch, "E304.MirrorCS", {"start": v(86.36, 20.07) * mm, "mid": v(83.83, 21.04) * mm, "end": v(83.08, 23.63) * mm});
            skArc(sketch, "E305.MirrorCS", {"start": v(-161.48, -82.91) * mm, "mid": v(-159.89, -80.73) * mm, "end": v(-157.19, -80.67) * mm});
            skArc(sketch, "E306.MirrorCS", {"start": v(-183.6, -62.77) * mm, "mid": v(-181.57, -61) * mm, "end": v(-178.92, -61.54) * mm});
            skArc(sketch, "E307.MirrorCS", {"start": v(-200.62, -40.26) * mm, "mid": v(-198.28, -38.92) * mm, "end": v(-195.79, -39.97) * mm});
            skArc(sketch, "E308.MirrorCS", {"start": v(68.11, -33.71) * mm, "mid": v(66.08, -31.94) * mm, "end": v(66.25, -29.24) * mm});
            skArc(sketch, "E309.MirrorCS", {"start": v(-113.23, -106.53) * mm, "mid": v(-111.84, -104.21) * mm, "end": v(-109.15, -103.92) * mm});
            skArc(sketch, "E310.MirrorCS", {"start": v(-139.49, -96.05) * mm, "mid": v(-137.82, -93.92) * mm, "end": v(-135.12, -93.96) * mm});
            skArc(sketch, "E311.MirrorCS", {"start": v(-93.65, -111.27) * mm, "mid": v(-92.68, -108.75) * mm, "end": v(-90.09, -108) * mm});
            skArc(sketch, "E312.MirrorCS", {"start": v(-223.74, 39.03) * mm, "mid": v(-221.05, 38.87) * mm, "end": v(-219.53, 36.63) * mm});
            skArc(sketch, "E313.MirrorCS", {"start": v(-212.58, -17.12) * mm, "mid": v(-210.07, -16.15) * mm, "end": v(-207.76, -17.55) * mm});
            skArc(sketch, "E314.MirrorCS", {"start": v(-219.54, 3.6) * mm, "mid": v(-216.92, 4.25) * mm, "end": v(-214.8, 2.56) * mm});
            skArc(sketch, "E315.MirrorCS", {"start": v(-22.64, -106.82) * mm, "mid": v(-22.95, -104.14) * mm, "end": v(-21, -102.26) * mm});
            skArc(sketch, "E316.MirrorCS", {"start": v(15.32, -89.36) * mm, "mid": v(14.44, -86.8) * mm, "end": v(15.94, -84.56) * mm});
            skArc(sketch, "E317.MirrorCS", {"start": v(33.54, -76.27) * mm, "mid": v(32.12, -73.98) * mm, "end": v(33.08, -71.45) * mm});
            skArc(sketch, "E318.MirrorCS", {"start": v(-46.02, -112.27) * mm, "mid": v(-46.2, -109.57) * mm, "end": v(-44.17, -107.79) * mm});
            skArc(sketch, "E319.MirrorCS", {"start": v(79.02, 1.93) * mm, "mid": v(81, 3.8) * mm, "end": v(83.7, 3.33) * mm});
            skArc(sketch, "E320.MirrorCS", {"start": v(83.91, 28.36) * mm, "mid": v(85.54, 30.56) * mm, "end": v(88.27, 30.56) * mm});
            skArc(sketch, "E321.MirrorCS", {"start": v(68.65, -25.08) * mm, "mid": v(70.94, -23.58) * mm, "end": v(73.5, -24.5) * mm});
            skArc(sketch, "E322.MirrorCS", {"start": v(-104.64, -105.56) * mm, "mid": v(-102.76, -107.54) * mm, "end": v(-103.23, -110.24) * mm});
            skArc(sketch, "E323.MirrorCS", {"start": v(-130.84, -96.14) * mm, "mid": v(-129.22, -98.34) * mm, "end": v(-130.02, -100.96) * mm});
            skArc(sketch, "E324.MirrorCS", {"start": v(-85.36, -108.83) * mm, "mid": v(-83.17, -110.46) * mm, "end": v(-83.16, -113.19) * mm});
            skLineSegment(sketch, "E325", {"start": v(241.37, 130.1) * mm, "end": v(242.45, 129.8) * mm});
            skLineSegment(sketch, "E326", {"start": v(244.7, 126.95) * mm, "end": v(244.88, 120.17) * mm});
            skLineSegment(sketch, "E327", {"start": v(237.95, 128.69) * mm, "end": v(234.56, 122.87) * mm});
            skLineSegment(sketch, "E328", {"start": v(236.4, 118.4) * mm, "end": v(241.05, 117.15) * mm});
            skArc(sketch, "E329.filletArc", {"start": v(244.7, 126.95) * mm, "mid": v(244.05, 128.75) * mm, "end": v(242.45, 129.8) * mm});
            skArc(sketch, "E330.filletArc", {"start": v(241.37, 130.1) * mm, "mid": v(239.42, 129.97) * mm, "end": v(237.95, 128.69) * mm});
            skArc(sketch, "E331.filletArc", {"start": v(241.05, 117.15) * mm, "mid": v(243.72, 117.7) * mm, "end": v(244.88, 120.17) * mm});
            skArc(sketch, "E332.filletArc", {"start": v(234.56, 122.87) * mm, "mid": v(234.38, 120.17) * mm, "end": v(236.4, 118.4) * mm});
            skLineSegment(sketch, "E333", {"start": v(272.71, 118.84) * mm, "end": v(273.65, 118.25) * mm});
            skLineSegment(sketch, "E334", {"start": v(274.97, 114.86) * mm, "end": v(273.16, 108.33) * mm});
            skLineSegment(sketch, "E335", {"start": v(269.03, 118.5) * mm, "end": v(264.08, 113.92) * mm});
            skLineSegment(sketch, "E336", {"start": v(264.54, 109.1) * mm, "end": v(268.61, 106.55) * mm});
            skArc(sketch, "E337.filletArc", {"start": v(274.97, 114.86) * mm, "mid": v(274.88, 116.77) * mm, "end": v(273.65, 118.25) * mm});
            skArc(sketch, "E338.filletArc", {"start": v(272.71, 118.84) * mm, "mid": v(270.8, 119.3) * mm, "end": v(269.03, 118.5) * mm});
            skArc(sketch, "E339.filletArc", {"start": v(268.61, 106.55) * mm, "mid": v(271.33, 106.3) * mm, "end": v(273.16, 108.33) * mm});
            skArc(sketch, "E340.filletArc", {"start": v(264.08, 113.92) * mm, "mid": v(263.12, 111.4) * mm, "end": v(264.54, 109.1) * mm});
            skLineSegment(sketch, "E341", {"start": v(293.25, 101.82) * mm, "end": v(293.97, 100.98) * mm});
            skLineSegment(sketch, "E342", {"start": v(294.2, 97.34) * mm, "end": v(290.52, 91.66) * mm});
            skLineSegment(sketch, "E343", {"start": v(289.63, 102.6) * mm, "end": v(283.54, 99.73) * mm});
            skLineSegment(sketch, "E344", {"start": v(282.52, 95) * mm, "end": v(285.64, 91.34) * mm});
            skArc(sketch, "E345.filletArc", {"start": v(294.2, 97.34) * mm, "mid": v(294.7, 99.2) * mm, "end": v(293.97, 100.98) * mm});
            skArc(sketch, "E346.filletArc", {"start": v(293.25, 101.82) * mm, "mid": v(291.57, 102.82) * mm, "end": v(289.63, 102.6) * mm});
            skArc(sketch, "E347.filletArc", {"start": v(285.64, 91.34) * mm, "mid": v(288.16, 90.28) * mm, "end": v(290.52, 91.66) * mm});
            skArc(sketch, "E348.filletArc", {"start": v(283.54, 99.73) * mm, "mid": v(281.86, 97.61) * mm, "end": v(282.52, 95) * mm});
            skLineSegment(sketch, "E349", {"start": v(308.62, 77.43) * mm, "end": v(309, 76.39) * mm});
            skLineSegment(sketch, "E350", {"start": v(307.95, 72.9) * mm, "end": v(302.5, 68.86) * mm});
            skLineSegment(sketch, "E351", {"start": v(305.5, 79.42) * mm, "end": v(298.8, 78.86) * mm});
            skLineSegment(sketch, "E352", {"start": v(296.18, 74.78) * mm, "end": v(297.83, 70.27) * mm});
            skArc(sketch, "E353.filletArc", {"start": v(307.95, 72.9) * mm, "mid": v(309.05, 74.47) * mm, "end": v(309, 76.39) * mm});
            skArc(sketch, "E354.filletArc", {"start": v(308.62, 77.43) * mm, "mid": v(307.4, 78.95) * mm, "end": v(305.5, 79.42) * mm});
            skArc(sketch, "E355.filletArc", {"start": v(297.83, 70.27) * mm, "mid": v(299.81, 68.4) * mm, "end": v(302.5, 68.86) * mm});
            skArc(sketch, "E356.filletArc", {"start": v(298.8, 78.86) * mm, "mid": v(296.48, 77.47) * mm, "end": v(296.18, 74.78) * mm});
            skLineSegment(sketch, "E357", {"start": v(315.16, 52.9) * mm, "end": v(315.26, 51.8) * mm});
            skLineSegment(sketch, "E358", {"start": v(313.34, 48.7) * mm, "end": v(307.04, 46.21) * mm});
            skLineSegment(sketch, "E359", {"start": v(312.67, 55.64) * mm, "end": v(306.04, 56.83) * mm});
            skLineSegment(sketch, "E360", {"start": v(302.46, 53.57) * mm, "end": v(302.88, 48.78) * mm});
            skArc(sketch, "E361.filletArc", {"start": v(313.34, 48.7) * mm, "mid": v(314.81, 49.93) * mm, "end": v(315.26, 51.8) * mm});
            skArc(sketch, "E362.filletArc", {"start": v(315.16, 52.9) * mm, "mid": v(314.38, 54.7) * mm, "end": v(312.67, 55.64) * mm});
            skArc(sketch, "E363.filletArc", {"start": v(302.88, 48.78) * mm, "mid": v(304.32, 46.45) * mm, "end": v(307.04, 46.21) * mm});
            skArc(sketch, "E364.filletArc", {"start": v(306.04, 56.83) * mm, "mid": v(303.45, 56.08) * mm, "end": v(302.46, 53.57) * mm});
            skLineSegment(sketch, "E365.MirrorCS", {"start": v(209.2, 129.15) * mm, "end": v(208.12, 128.87) * mm});
            skLineSegment(sketch, "E366.MirrorCS", {"start": v(181.35, 118.84) * mm, "end": v(180.41, 118.25) * mm});
            skLineSegment(sketch, "E367.MirrorCS", {"start": v(145.45, 77.43) * mm, "end": v(145.07, 76.39) * mm});
            skArc(sketch, "E368.MirrorCS", {"start": v(209.2, 129.15) * mm, "mid": v(211.14, 129.03) * mm, "end": v(212.62, 127.74) * mm});
            skArc(sketch, "E369.MirrorCS", {"start": v(205.86, 126) * mm, "mid": v(206.52, 127.81) * mm, "end": v(208.12, 128.87) * mm});
            skArc(sketch, "E370.MirrorCS", {"start": v(159.86, 97.34) * mm, "mid": v(159.37, 99.2) * mm, "end": v(160.1, 100.98) * mm});
            skArc(sketch, "E371.MirrorCS", {"start": v(140.72, 48.7) * mm, "mid": v(139.25, 49.93) * mm, "end": v(138.8, 51.8) * mm});
            skLineSegment(sketch, "E372.MirrorCS", {"start": v(160.82, 101.82) * mm, "end": v(160.1, 100.98) * mm});
            skLineSegment(sketch, "E373.MirrorCS", {"start": v(138.9, 52.9) * mm, "end": v(138.8, 51.8) * mm});
            skArc(sketch, "E374.MirrorCS", {"start": v(185.45, 106.55) * mm, "mid": v(182.73, 106.3) * mm, "end": v(180.9, 108.33) * mm});
            skArc(sketch, "E375.MirrorCS", {"start": v(181.35, 118.84) * mm, "mid": v(183.26, 119.3) * mm, "end": v(185.04, 118.5) * mm});
            skArc(sketch, "E376.MirrorCS", {"start": v(146.12, 72.9) * mm, "mid": v(145.01, 74.47) * mm, "end": v(145.07, 76.39) * mm});
            skArc(sketch, "E377.MirrorCS", {"start": v(179.1, 114.86) * mm, "mid": v(179.19, 116.77) * mm, "end": v(180.41, 118.25) * mm});
            skArc(sketch, "E378.MirrorCS", {"start": v(216, 121.93) * mm, "mid": v(216.19, 119.23) * mm, "end": v(214.16, 117.45) * mm});
            skArc(sketch, "E379.MirrorCS", {"start": v(170.52, 99.73) * mm, "mid": v(172.2, 97.61) * mm, "end": v(171.54, 95) * mm});
            skArc(sketch, "E380.MirrorCS", {"start": v(148.02, 56.83) * mm, "mid": v(150.62, 56.08) * mm, "end": v(151.6, 53.57) * mm});
            skArc(sketch, "E381.MirrorCS", {"start": v(209.52, 116.2) * mm, "mid": v(206.84, 116.76) * mm, "end": v(205.68, 119.23) * mm});
            skArc(sketch, "E382.MirrorCS", {"start": v(168.42, 91.34) * mm, "mid": v(165.9, 90.28) * mm, "end": v(163.55, 91.66) * mm});
            skArc(sketch, "E383.MirrorCS", {"start": v(151.18, 48.78) * mm, "mid": v(149.75, 46.45) * mm, "end": v(147.03, 46.21) * mm});
            skArc(sketch, "E384.MirrorCS", {"start": v(160.82, 101.82) * mm, "mid": v(162.5, 102.82) * mm, "end": v(164.44, 102.6) * mm});
            skArc(sketch, "E385.MirrorCS", {"start": v(138.9, 52.9) * mm, "mid": v(139.69, 54.7) * mm, "end": v(141.4, 55.64) * mm});
            skLineSegment(sketch, "E386.MirrorCS", {"start": v(214.16, 117.45) * mm, "end": v(209.52, 116.2) * mm});
            skLineSegment(sketch, "E387.MirrorCS", {"start": v(171.54, 95) * mm, "end": v(168.42, 91.34) * mm});
            skLineSegment(sketch, "E388.MirrorCS", {"start": v(151.6, 53.57) * mm, "end": v(151.18, 48.78) * mm});
            skLineSegment(sketch, "E389.MirrorCS", {"start": v(141.4, 55.64) * mm, "end": v(148.02, 56.83) * mm});
            skLineSegment(sketch, "E390.MirrorCS", {"start": v(212.62, 127.74) * mm, "end": v(216, 121.93) * mm});
            skLineSegment(sketch, "E391.MirrorCS", {"start": v(164.44, 102.6) * mm, "end": v(170.52, 99.73) * mm});
            skLineSegment(sketch, "E392.MirrorCS", {"start": v(140.72, 48.7) * mm, "end": v(147.03, 46.21) * mm});
            skLineSegment(sketch, "E393.MirrorCS", {"start": v(205.86, 126) * mm, "end": v(205.68, 119.23) * mm});
            skLineSegment(sketch, "E394.MirrorCS", {"start": v(159.86, 97.34) * mm, "end": v(163.55, 91.66) * mm});
            skArc(sketch, "E395.MirrorCS", {"start": v(155.27, 78.86) * mm, "mid": v(157.59, 77.47) * mm, "end": v(157.88, 74.78) * mm});
            skArc(sketch, "E396.MirrorCS", {"start": v(189.98, 113.92) * mm, "mid": v(190.95, 111.4) * mm, "end": v(189.53, 109.1) * mm});
            skArc(sketch, "E397.MirrorCS", {"start": v(156.24, 70.27) * mm, "mid": v(154.25, 68.4) * mm, "end": v(151.56, 68.86) * mm});
            skArc(sketch, "E398.MirrorCS", {"start": v(145.45, 77.43) * mm, "mid": v(146.67, 78.95) * mm, "end": v(148.56, 79.42) * mm});
            skLineSegment(sketch, "E399.MirrorCS", {"start": v(157.88, 74.78) * mm, "end": v(156.24, 70.27) * mm});
            skLineSegment(sketch, "E400.MirrorCS", {"start": v(189.53, 109.1) * mm, "end": v(185.45, 106.55) * mm});
            skLineSegment(sketch, "E401.MirrorCS", {"start": v(148.56, 79.42) * mm, "end": v(155.27, 78.86) * mm});
            skLineSegment(sketch, "E402.MirrorCS", {"start": v(185.04, 118.5) * mm, "end": v(189.98, 113.92) * mm});
            skLineSegment(sketch, "E403.MirrorCS", {"start": v(179.1, 114.86) * mm, "end": v(180.9, 108.33) * mm});
            skLineSegment(sketch, "E404.MirrorCS", {"start": v(146.12, 72.9) * mm, "end": v(151.56, 68.86) * mm});
            skLineSegment(sketch, "E405.MirrorCS", {"start": v(293.25, -16.28) * mm, "end": v(293.97, -15.44) * mm});
            skLineSegment(sketch, "E406.MirrorCS", {"start": v(241.37, -44.56) * mm, "end": v(242.45, -44.27) * mm});
            skArc(sketch, "E407.MirrorCS", {"start": v(294.2, -11.8) * mm, "mid": v(294.7, -13.66) * mm, "end": v(293.97, -15.44) * mm});
            skLineSegment(sketch, "E408.MirrorCS", {"start": v(181.35, -33.3) * mm, "end": v(180.41, -32.71) * mm});
            skLineSegment(sketch, "E409.MirrorCS", {"start": v(315.16, 32.64) * mm, "end": v(315.26, 33.74) * mm});
            skArc(sketch, "E410.MirrorCS", {"start": v(181.35, -33.3) * mm, "mid": v(183.26, -33.75) * mm, "end": v(185.04, -32.96) * mm});
            skArc(sketch, "E411.MirrorCS", {"start": v(179.1, -29.32) * mm, "mid": v(179.19, -31.23) * mm, "end": v(180.41, -32.71) * mm});
            skArc(sketch, "E412.MirrorCS", {"start": v(313.34, 36.84) * mm, "mid": v(314.81, 35.61) * mm, "end": v(315.26, 33.74) * mm});
            skArc(sketch, "E413.MirrorCS", {"start": v(244.7, -41.4) * mm, "mid": v(244.05, -43.21) * mm, "end": v(242.45, -44.27) * mm});
            skArc(sketch, "E414.MirrorCS", {"start": v(315.16, 32.64) * mm, "mid": v(314.38, 30.85) * mm, "end": v(312.67, 29.9) * mm});
            skArc(sketch, "E415.MirrorCS", {"start": v(293.25, -16.28) * mm, "mid": v(291.57, -17.28) * mm, "end": v(289.63, -17.06) * mm});
            skArc(sketch, "E416.MirrorCS", {"start": v(241.37, -44.56) * mm, "mid": v(239.42, -44.43) * mm, "end": v(237.95, -43.15) * mm});
            skLineSegment(sketch, "E417.MirrorCS", {"start": v(308.62, 8.11) * mm, "end": v(309, 9.15) * mm});
            skLineSegment(sketch, "E418.MirrorCS", {"start": v(272.71, -33.3) * mm, "end": v(273.65, -32.71) * mm});
            skArc(sketch, "E419.MirrorCS", {"start": v(274.97, -29.32) * mm, "mid": v(274.88, -31.23) * mm, "end": v(273.65, -32.71) * mm});
            skLineSegment(sketch, "E420.MirrorCS", {"start": v(141.4, 29.9) * mm, "end": v(148.02, 28.7) * mm});
            skLineSegment(sketch, "E421.MirrorCS", {"start": v(138.9, 32.64) * mm, "end": v(138.8, 33.74) * mm});
            skLineSegment(sketch, "E422.MirrorCS", {"start": v(294.2, -11.8) * mm, "end": v(290.52, -6.12) * mm});
            skLineSegment(sketch, "E423.MirrorCS", {"start": v(244.7, -41.4) * mm, "end": v(244.88, -34.63) * mm});
            skLineSegment(sketch, "E424.MirrorCS", {"start": v(212.62, -42.2) * mm, "end": v(216, -36.39) * mm});
            skArc(sketch, "E425.MirrorCS", {"start": v(185.45, -21.02) * mm, "mid": v(182.73, -20.76) * mm, "end": v(180.9, -22.79) * mm});
            skLineSegment(sketch, "E426.MirrorCS", {"start": v(313.34, 36.84) * mm, "end": v(307.04, 39.33) * mm});
            skLineSegment(sketch, "E427.MirrorCS", {"start": v(269.03, -32.96) * mm, "end": v(264.08, -28.38) * mm});
            skLineSegment(sketch, "E428.MirrorCS", {"start": v(289.63, -17.06) * mm, "end": v(283.54, -14.19) * mm});
            skLineSegment(sketch, "E429.MirrorCS", {"start": v(237.95, -43.15) * mm, "end": v(234.56, -37.33) * mm});
            skLineSegment(sketch, "E430.MirrorCS", {"start": v(164.44, -17.06) * mm, "end": v(170.52, -14.19) * mm});
            skLineSegment(sketch, "E431.MirrorCS", {"start": v(312.67, 29.9) * mm, "end": v(306.04, 28.7) * mm});
            skLineSegment(sketch, "E432.MirrorCS", {"start": v(157.88, 10.76) * mm, "end": v(156.24, 15.27) * mm});
            skArc(sketch, "E433.MirrorCS", {"start": v(146.12, 12.65) * mm, "mid": v(145.01, 11.07) * mm, "end": v(145.07, 9.15) * mm});
            skLineSegment(sketch, "E434.MirrorCS", {"start": v(302.46, 31.97) * mm, "end": v(302.88, 36.76) * mm});
            skLineSegment(sketch, "E435.MirrorCS", {"start": v(282.52, -9.45) * mm, "end": v(285.64, -5.8) * mm});
            skLineSegment(sketch, "E436.MirrorCS", {"start": v(236.4, -32.85) * mm, "end": v(241.05, -31.6) * mm});
            skLineSegment(sketch, "E437.MirrorCS", {"start": v(140.72, 36.84) * mm, "end": v(147.03, 39.33) * mm});
            skArc(sketch, "E438.MirrorCS", {"start": v(151.18, 36.76) * mm, "mid": v(149.75, 39.09) * mm, "end": v(147.03, 39.33) * mm});
            skLineSegment(sketch, "E439.MirrorCS", {"start": v(145.45, 8.11) * mm, "end": v(145.07, 9.15) * mm});
            skLineSegment(sketch, "E440.MirrorCS", {"start": v(305.5, 6.12) * mm, "end": v(298.8, 6.68) * mm});
            skLineSegment(sketch, "E441.MirrorCS", {"start": v(205.86, -40.46) * mm, "end": v(205.68, -33.7) * mm});
            skArc(sketch, "E442.MirrorCS", {"start": v(216, -36.39) * mm, "mid": v(216.19, -33.7) * mm, "end": v(214.16, -31.9) * mm});
            skLineSegment(sketch, "E443.MirrorCS", {"start": v(159.86, -11.8) * mm, "end": v(163.55, -6.12) * mm});
            skArc(sketch, "E444.MirrorCS", {"start": v(170.52, -14.19) * mm, "mid": v(172.2, -12.07) * mm, "end": v(171.54, -9.45) * mm});
            skArc(sketch, "E445.MirrorCS", {"start": v(302.88, 36.76) * mm, "mid": v(304.32, 39.09) * mm, "end": v(307.04, 39.33) * mm});
            skArc(sketch, "E446.MirrorCS", {"start": v(285.64, -5.8) * mm, "mid": v(288.16, -4.74) * mm, "end": v(290.52, -6.12) * mm});
            skArc(sketch, "E447.MirrorCS", {"start": v(241.05, -31.6) * mm, "mid": v(243.72, -32.16) * mm, "end": v(244.88, -34.63) * mm});
            skArc(sketch, "E448.MirrorCS", {"start": v(155.27, 6.68) * mm, "mid": v(157.59, 8.07) * mm, "end": v(157.88, 10.76) * mm});
            skArc(sketch, "E449.MirrorCS", {"start": v(148.02, 28.7) * mm, "mid": v(150.62, 29.46) * mm, "end": v(151.6, 31.97) * mm});
            skArc(sketch, "E450.MirrorCS", {"start": v(306.04, 28.7) * mm, "mid": v(303.45, 29.46) * mm, "end": v(302.46, 31.97) * mm});
            skArc(sketch, "E451.MirrorCS", {"start": v(283.54, -14.19) * mm, "mid": v(281.86, -12.07) * mm, "end": v(282.52, -9.45) * mm});
            skArc(sketch, "E452.MirrorCS", {"start": v(234.56, -37.33) * mm, "mid": v(234.38, -34.63) * mm, "end": v(236.4, -32.85) * mm});
            skArc(sketch, "E453.MirrorCS", {"start": v(189.98, -28.38) * mm, "mid": v(190.95, -25.86) * mm, "end": v(189.53, -23.56) * mm});
            skArc(sketch, "E454.MirrorCS", {"start": v(209.52, -30.67) * mm, "mid": v(206.84, -31.22) * mm, "end": v(205.68, -33.7) * mm});
            skArc(sketch, "E455.MirrorCS", {"start": v(264.08, -28.38) * mm, "mid": v(263.12, -25.86) * mm, "end": v(264.54, -23.56) * mm});
            skLineSegment(sketch, "E456.MirrorCS", {"start": v(209.2, -43.62) * mm, "end": v(208.12, -43.33) * mm});
            skArc(sketch, "E457.MirrorCS", {"start": v(156.24, 15.27) * mm, "mid": v(154.25, 17.15) * mm, "end": v(151.56, 16.68) * mm});
            skLineSegment(sketch, "E458.MirrorCS", {"start": v(146.12, 12.65) * mm, "end": v(151.56, 16.68) * mm});
            skLineSegment(sketch, "E459.MirrorCS", {"start": v(151.6, 31.97) * mm, "end": v(151.18, 36.76) * mm});
            skLineSegment(sketch, "E460.MirrorCS", {"start": v(160.82, -16.28) * mm, "end": v(160.1, -15.44) * mm});
            skArc(sketch, "E461.MirrorCS", {"start": v(298.8, 6.68) * mm, "mid": v(296.48, 8.07) * mm, "end": v(296.18, 10.76) * mm});
            skArc(sketch, "E462.MirrorCS", {"start": v(308.62, 8.11) * mm, "mid": v(307.4, 6.59) * mm, "end": v(305.5, 6.12) * mm});
            skArc(sketch, "E463.MirrorCS", {"start": v(209.2, -43.62) * mm, "mid": v(211.14, -43.49) * mm, "end": v(212.62, -42.2) * mm});
            skArc(sketch, "E464.MirrorCS", {"start": v(160.82, -16.28) * mm, "mid": v(162.5, -17.28) * mm, "end": v(164.44, -17.06) * mm});
            skLineSegment(sketch, "E465.MirrorCS", {"start": v(189.53, -23.56) * mm, "end": v(185.45, -21.02) * mm});
            skLineSegment(sketch, "E466.MirrorCS", {"start": v(296.18, 10.76) * mm, "end": v(297.83, 15.27) * mm});
            skLineSegment(sketch, "E467.MirrorCS", {"start": v(264.54, -23.56) * mm, "end": v(268.61, -21.02) * mm});
            skArc(sketch, "E468.MirrorCS", {"start": v(268.61, -21.02) * mm, "mid": v(271.33, -20.76) * mm, "end": v(273.16, -22.79) * mm});
            skLineSegment(sketch, "E469.MirrorCS", {"start": v(179.1, -29.32) * mm, "end": v(180.9, -22.79) * mm});
            skArc(sketch, "E470.MirrorCS", {"start": v(297.83, 15.27) * mm, "mid": v(299.81, 17.15) * mm, "end": v(302.5, 16.68) * mm});
            skLineSegment(sketch, "E471.MirrorCS", {"start": v(171.54, -9.45) * mm, "end": v(168.42, -5.8) * mm});
            skArc(sketch, "E472.MirrorCS", {"start": v(140.72, 36.84) * mm, "mid": v(139.25, 35.61) * mm, "end": v(138.8, 33.74) * mm});
            skLineSegment(sketch, "E473.MirrorCS", {"start": v(274.97, -29.32) * mm, "end": v(273.16, -22.79) * mm});
            skLineSegment(sketch, "E474.MirrorCS", {"start": v(214.16, -31.9) * mm, "end": v(209.52, -30.67) * mm});
            skArc(sketch, "E475.MirrorCS", {"start": v(159.86, -11.8) * mm, "mid": v(159.37, -13.66) * mm, "end": v(160.1, -15.44) * mm});
            skLineSegment(sketch, "E476.MirrorCS", {"start": v(185.04, -32.96) * mm, "end": v(189.98, -28.38) * mm});
            skArc(sketch, "E477.MirrorCS", {"start": v(145.45, 8.11) * mm, "mid": v(146.67, 6.59) * mm, "end": v(148.56, 6.12) * mm});
            skArc(sketch, "E478.MirrorCS", {"start": v(168.42, -5.8) * mm, "mid": v(165.9, -4.74) * mm, "end": v(163.55, -6.12) * mm});
            skLineSegment(sketch, "E479.MirrorCS", {"start": v(307.95, 12.65) * mm, "end": v(302.5, 16.68) * mm});
            skArc(sketch, "E480.MirrorCS", {"start": v(307.95, 12.65) * mm, "mid": v(309.05, 11.07) * mm, "end": v(309, 9.15) * mm});
            skArc(sketch, "E481.MirrorCS", {"start": v(138.9, 32.64) * mm, "mid": v(139.69, 30.85) * mm, "end": v(141.4, 29.9) * mm});
            skArc(sketch, "E482.MirrorCS", {"start": v(205.86, -40.46) * mm, "mid": v(206.52, -42.27) * mm, "end": v(208.12, -43.33) * mm});
            skLineSegment(sketch, "E483.MirrorCS", {"start": v(148.56, 6.12) * mm, "end": v(155.27, 6.68) * mm});
            skArc(sketch, "E484.MirrorCS", {"start": v(272.71, -33.3) * mm, "mid": v(270.8, -33.75) * mm, "end": v(269.03, -32.96) * mm});
            skSolve(sketch);
        }
        {
            var Q0;
            Q0=makeQuery(id+"F0.imprint","IMPRINT",FACE,{"disambiguationData":[TD([[makeQuery(id+"F0.imprint","IMPRINT",EDGE,{"derivedFrom":sQuery(id+"F0.wireOp",EDGE,"E2")}),-1.0]])]});
            var Q1;
            Q1=makeQuery(id+"F0.imprint","IMPRINT",FACE,{"disambiguationData":[TD([[makeQuery(id+"F0.imprint","IMPRINT",EDGE,{"derivedFrom":sQuery(id+"F0.wireOp",EDGE,"E93")}),-1.0]])]});
            var Q2;
            Q2=makeQuery(id+"F0.imprint","IMPRINT",FACE,{"disambiguationData":[TD([[makeQuery(id+"F0.imprint","IMPRINT",EDGE,{"derivedFrom":sQuery(id+"F0.wireOp",EDGE,"E175.MirrorCS")}),1.0]])]});
            var Q3;
            Q3=makeQuery(id+"F0.imprint","IMPRINT",FACE,{"disambiguationData":[TD([[makeQuery(id+"F0.imprint","IMPRINT",EDGE,{"derivedFrom":sQuery(id+"F0.wireOp",EDGE,"E125")}),-1.0]])]});
            var Q4;
            Q4=makeQuery(id+"F0.imprint","IMPRINT",FACE,{"disambiguationData":[TD([[makeQuery(id+"F0.imprint","IMPRINT",EDGE,{"derivedFrom":sQuery(id+"F0.wireOp",EDGE,"E179.MirrorCS")}),1.0]])]});
            var Q5;
            Q5=makeQuery(id+"F0.imprint","IMPRINT",FACE,{"disambiguationData":[TD([[makeQuery(id+"F0.imprint","IMPRINT",EDGE,{"derivedFrom":sQuery(id+"F0.wireOp",EDGE,"E193.MirrorCS")}),1.0]])]});
            var Q6;
            Q6=makeQuery(id+"F0.imprint","IMPRINT",FACE,{"disambiguationData":[TD([[makeQuery(id+"F0.imprint","IMPRINT",EDGE,{"derivedFrom":sQuery(id+"F0.wireOp",EDGE,"E178.MirrorCS")}),1.0]])]});
            var Q7;
            Q7=makeQuery(id+"F0.imprint","IMPRINT",FACE,{"disambiguationData":[TD([[makeQuery(id+"F0.imprint","IMPRINT",EDGE,{"derivedFrom":sQuery(id+"F0.wireOp",EDGE,"E180.MirrorCS")}),1.0]])]});
            var Q8;
            Q8=makeQuery(id+"F0.imprint","IMPRINT",FACE,{"disambiguationData":[TD([[makeQuery(id+"F0.imprint","IMPRINT",EDGE,{"derivedFrom":sQuery(id+"F0.wireOp",EDGE,"E199.MirrorCS")}),1.0]])]});
            var Q9;
            Q9=makeQuery(id+"F0.imprint","IMPRINT",FACE,{"disambiguationData":[TD([[makeQuery(id+"F0.imprint","IMPRINT",EDGE,{"derivedFrom":sQuery(id+"F0.wireOp",EDGE,"E207.MirrorCS")}),-1.0]])]});
            var Q10;
            Q10=makeQuery(id+"F0.imprint","IMPRINT",FACE,{"disambiguationData":[TD([[makeQuery(id+"F0.imprint","IMPRINT",EDGE,{"derivedFrom":sQuery(id+"F0.wireOp",EDGE,"E29")}),-1.0]])]});
            var Q11;
            Q11=makeQuery(id+"F0.imprint","IMPRINT",FACE,{"disambiguationData":[TD([[makeQuery(id+"F0.imprint","IMPRINT",EDGE,{"derivedFrom":sQuery(id+"F0.wireOp",EDGE,"E77")}),-1.0]])]});
            var Q12;
            Q12=makeQuery(id+"F0.imprint","IMPRINT",FACE,{"disambiguationData":[TD([[makeQuery(id+"F0.imprint","IMPRINT",EDGE,{"derivedFrom":sQuery(id+"F0.wireOp",EDGE,"E197.MirrorCS")}),1.0]])]});
            var Q13;
            Q13=makeQuery(id+"F0.imprint","IMPRINT",FACE,{"disambiguationData":[TD([[makeQuery(id+"F0.imprint","IMPRINT",EDGE,{"derivedFrom":sQuery(id+"F0.wireOp",EDGE,"E101")}),-1.0]])]});
            var Q14;
            Q14=makeQuery(id+"F0.imprint","IMPRINT",FACE,{"disambiguationData":[TD([[makeQuery(id+"F0.imprint","IMPRINT",EDGE,{"derivedFrom":sQuery(id+"F0.wireOp",EDGE,"E69")}),-1.0]])]});
            var Q15;
            Q15=makeQuery(id+"F0.imprint","IMPRINT",FACE,{"disambiguationData":[TD([[makeQuery(id+"F0.imprint","IMPRINT",EDGE,{"derivedFrom":sQuery(id+"F0.wireOp",EDGE,"E133")}),-1.0]])]});
            var Q16;
            Q16=makeQuery(id+"F0.imprint","IMPRINT",FACE,{"disambiguationData":[TD([[makeQuery(id+"F0.imprint","IMPRINT",EDGE,{"derivedFrom":sQuery(id+"F0.wireOp",EDGE,"E167.MirrorCS")}),1.0]])]});
            var Q17;
            Q17=makeQuery(id+"F0.imprint","IMPRINT",FACE,{"disambiguationData":[TD([[makeQuery(id+"F0.imprint","IMPRINT",EDGE,{"derivedFrom":sQuery(id+"F0.wireOp",EDGE,"E198.MirrorCS")}),1.0]])]});
            var Q18;
            Q18=makeQuery(id+"F0.imprint","IMPRINT",FACE,{"disambiguationData":[TD([[makeQuery(id+"F0.imprint","IMPRINT",EDGE,{"derivedFrom":sQuery(id+"F0.wireOp",EDGE,"E45")}),-1.0]])]});
            var Q19;
            Q19=makeQuery(id+"F0.imprint","IMPRINT",FACE,{"disambiguationData":[TD([[makeQuery(id+"F0.imprint","IMPRINT",EDGE,{"derivedFrom":sQuery(id+"F0.wireOp",EDGE,"E61")}),-1.0]])]});
            var Q20;
            {var subQ0=sQuery(id+"F0.wireOp",EDGE,"E160");Q20=makeQuery(id+"F0.imprint","IMPRINT",FACE,{"disambiguationData":[TD([[makeQuery(id+"F0.imprint","IMPRINT",EDGE,{"derivedFrom":subQ0}),1.0]])]});}
            var Q21;
            Q21=makeQuery(id+"F0.imprint","IMPRINT",FACE,{"disambiguationData":[TD([[makeQuery(id+"F0.imprint","IMPRINT",EDGE,{"derivedFrom":sQuery(id+"F0.wireOp",EDGE,"E195.MirrorCS")}),1.0]])]});
            var Q22;
            Q22=makeQuery(id+"F0.imprint","IMPRINT",FACE,{"disambiguationData":[TD([[makeQuery(id+"F0.imprint","IMPRINT",EDGE,{"derivedFrom":sQuery(id+"F0.wireOp",EDGE,"E21")}),-1.0]])]});
            var Q23;
            Q23=makeQuery(id+"F0.imprint","IMPRINT",FACE,{"disambiguationData":[TD([[makeQuery(id+"F0.imprint","IMPRINT",EDGE,{"derivedFrom":sQuery(id+"F0.wireOp",EDGE,"E37")}),-1.0]])]});
            var Q24;
            Q24=makeQuery(id+"F0.imprint","IMPRINT",FACE,{"disambiguationData":[TD([[makeQuery(id+"F0.imprint","IMPRINT",EDGE,{"derivedFrom":sQuery(id+"F0.wireOp",EDGE,"E166.MirrorCS")}),1.0]])]});
            var Q25;
            {var subQ0=sQuery(id+"F0.wireOp",EDGE,"E128");Q25=makeQuery(id+"F0.imprint","IMPRINT",FACE,{"disambiguationData":[TD([[makeQuery(id+"F0.imprint","IMPRINT",EDGE,{"derivedFrom":subQ0}),1.0]])]});}
            var Q26;
            {var subQ0=sQuery(id+"F0.wireOp",EDGE,"E264.MirrorCS");Q26=makeQuery(id+"F0.imprint","IMPRINT",FACE,{"disambiguationData":[TD([[makeQuery(id+"F0.imprint","IMPRINT",EDGE,{"derivedFrom":subQ0}),-1.0]])]});}
            var Q27;
            Q27=makeQuery(id+"F0.imprint","IMPRINT",FACE,{"disambiguationData":[TD([[makeQuery(id+"F0.imprint","IMPRINT",EDGE,{"derivedFrom":sQuery(id+"F0.wireOp",EDGE,"E212.MirrorCS")}),-1.0]])]});
            var Q28;
            Q28=makeQuery(id+"F0.imprint","IMPRINT",FACE,{"disambiguationData":[TD([[makeQuery(id+"F0.imprint","IMPRINT",EDGE,{"derivedFrom":sQuery(id+"F0.wireOp",EDGE,"E209.MirrorCS")}),-1.0]])]});
            var Q29;
            {var subQ0=sQuery(id+"F0.wireOp",EDGE,"E136");Q29=makeQuery(id+"F0.imprint","IMPRINT",FACE,{"disambiguationData":[TD([[makeQuery(id+"F0.imprint","IMPRINT",EDGE,{"derivedFrom":subQ0}),1.0]])]});}
            var Q30;
            {var subQ0=sQuery(id+"F0.wireOp",EDGE,"E100.filletArc");var subQ1=sQuery(id+"F0.wireOp",EDGE,"E0");var subQ3=makeQuery(id+"F0.imprint","INTERSECT",VERTEX,{"derivedFrom":[subQ1,subQ0]});Q30=makeQuery(id+"F0.imprint","IMPRINT",FACE,{"disambiguationData":[TD([[makeQuery(id+"F0.imprint","IMPRINT",EDGE,{"disambiguationData":[TD([[subQ3,1.0]])],"derivedFrom":subQ1}),1.0]])]});}
            var Q31;
            Q31=makeQuery(id+"F0.imprint","IMPRINT",FACE,{"disambiguationData":[TD([[makeQuery(id+"F0.imprint","IMPRINT",EDGE,{"derivedFrom":sQuery(id+"F0.wireOp",EDGE,"E109")}),-1.0]])]});
            var Q32;
            {var subQ0=sQuery(id+"F0.wireOp",EDGE,"E275.MirrorCS");Q32=makeQuery(id+"F0.imprint","IMPRINT",FACE,{"disambiguationData":[TD([[makeQuery(id+"F0.imprint","IMPRINT",EDGE,{"derivedFrom":subQ0}),-1.0]])]});}
            var Q33;
            {var subQ0=sQuery(id+"F0.wireOp",EDGE,"E80");Q33=makeQuery(id+"F0.imprint","IMPRINT",FACE,{"disambiguationData":[TD([[makeQuery(id+"F0.imprint","IMPRINT",EDGE,{"derivedFrom":subQ0}),1.0]])]});}
            var Q34;
            {var subQ0=sQuery(id+"F0.wireOp",EDGE,"E262.MirrorCS");Q34=makeQuery(id+"F0.imprint","IMPRINT",FACE,{"disambiguationData":[TD([[makeQuery(id+"F0.imprint","IMPRINT",EDGE,{"derivedFrom":subQ0}),-1.0]])]});}
            var Q35;
            Q35=makeQuery(id+"F0.imprint","IMPRINT",FACE,{"disambiguationData":[TD([[makeQuery(id+"F0.imprint","IMPRINT",EDGE,{"derivedFrom":sQuery(id+"F0.wireOp",EDGE,"E141")}),-1.0]])]});
            var Q36;
            {var subQ0=sQuery(id+"F0.wireOp",EDGE,"E263.MirrorCS");Q36=makeQuery(id+"F0.imprint","IMPRINT",FACE,{"disambiguationData":[TD([[makeQuery(id+"F0.imprint","IMPRINT",EDGE,{"derivedFrom":subQ0}),-1.0]])]});}
            var Q37;
            {var subQ0=sQuery(id+"F0.wireOp",EDGE,"E68.filletArc");var subQ1=sQuery(id+"F0.wireOp",EDGE,"E0");var subQ3=makeQuery(id+"F0.imprint","INTERSECT",VERTEX,{"derivedFrom":[subQ1,subQ0]});Q37=makeQuery(id+"F0.imprint","IMPRINT",FACE,{"disambiguationData":[TD([[makeQuery(id+"F0.imprint","IMPRINT",EDGE,{"disambiguationData":[TD([[subQ3,1.0]])],"derivedFrom":subQ1}),1.0]])]});}
            var Q38;
            Q38=makeQuery(id+"F0.imprint","IMPRINT",FACE,{"disambiguationData":[TD([[makeQuery(id+"F0.imprint","IMPRINT",EDGE,{"derivedFrom":sQuery(id+"F0.wireOp",EDGE,"E187.MirrorCS")}),-1.0]])]});
            var Q39;
            {var subQ0=sQuery(id+"F0.wireOp",EDGE,"E261.MirrorCS");Q39=makeQuery(id+"F0.imprint","IMPRINT",FACE,{"disambiguationData":[TD([[makeQuery(id+"F0.imprint","IMPRINT",EDGE,{"derivedFrom":subQ0}),-1.0]])]});}
            var Q40;
            Q40=makeQuery(id+"F0.imprint","IMPRINT",FACE,{"disambiguationData":[TD([[makeQuery(id+"F0.imprint","IMPRINT",EDGE,{"derivedFrom":sQuery(id+"F0.wireOp",EDGE,"E157")}),-1.0]])]});
            var Q41;
            {var subQ0=sQuery(id+"F0.wireOp",EDGE,"E286.MirrorCS");Q41=makeQuery(id+"F0.imprint","IMPRINT",FACE,{"disambiguationData":[TD([[makeQuery(id+"F0.imprint","IMPRINT",EDGE,{"derivedFrom":subQ0}),-1.0]])]});}
            var Q42;
            Q42=makeQuery(id+"F0.imprint","IMPRINT",FACE,{"disambiguationData":[TD([[makeQuery(id+"F0.imprint","IMPRINT",EDGE,{"derivedFrom":sQuery(id+"F0.wireOp",EDGE,"E211.MirrorCS")}),-1.0]])]});
            var Q43;
            {var subQ0=sQuery(id+"F0.wireOp",EDGE,"E72");Q43=makeQuery(id+"F0.imprint","IMPRINT",FACE,{"disambiguationData":[TD([[makeQuery(id+"F0.imprint","IMPRINT",EDGE,{"derivedFrom":subQ0}),1.0]])]});}
            var Q44;
            {var subQ0=sQuery(id+"F0.wireOp",EDGE,"E28.filletArc");var subQ1=sQuery(id+"F0.wireOp",EDGE,"E0");var subQ3=makeQuery(id+"F0.imprint","INTERSECT",VERTEX,{"derivedFrom":[subQ1,subQ0]});Q44=makeQuery(id+"F0.imprint","IMPRINT",FACE,{"disambiguationData":[TD([[makeQuery(id+"F0.imprint","IMPRINT",EDGE,{"disambiguationData":[TD([[subQ3,1.0]])],"derivedFrom":subQ1}),1.0]])]});}
            var Q45;
            Q45=makeQuery(id+"F0.imprint","IMPRINT",FACE,{"disambiguationData":[TD([[makeQuery(id+"F0.imprint","IMPRINT",EDGE,{"derivedFrom":sQuery(id+"F0.wireOp",EDGE,"E194.MirrorCS")}),1.0]])]});
            var Q46;
            Q46=makeQuery(id+"F0.imprint","IMPRINT",FACE,{"disambiguationData":[TD([[makeQuery(id+"F0.imprint","IMPRINT",EDGE,{"derivedFrom":sQuery(id+"F0.wireOp",EDGE,"E13")}),-1.0]])]});
            var Q47;
            Q47=makeQuery(id+"F0.imprint","IMPRINT",FACE,{"disambiguationData":[TD([[makeQuery(id+"F0.imprint","IMPRINT",EDGE,{"derivedFrom":sQuery(id+"F0.wireOp",EDGE,"E117")}),-1.0]])]});
            var Q48;
            Q48=makeQuery(id+"F0.imprint","IMPRINT",FACE,{"disambiguationData":[TD([[makeQuery(id+"F0.imprint","IMPRINT",EDGE,{"derivedFrom":sQuery(id+"F0.wireOp",EDGE,"E5")}),-1.0]])]});
            var Q49;
            {var subQ0=sQuery(id+"F0.wireOp",EDGE,"E104");Q49=makeQuery(id+"F0.imprint","IMPRINT",FACE,{"disambiguationData":[TD([[makeQuery(id+"F0.imprint","IMPRINT",EDGE,{"derivedFrom":subQ0}),1.0]])]});}
            var Q50;
            {var subQ0=sQuery(id+"F0.wireOp",EDGE,"E268.MirrorCS");Q50=makeQuery(id+"F0.imprint","IMPRINT",FACE,{"disambiguationData":[TD([[makeQuery(id+"F0.imprint","IMPRINT",EDGE,{"derivedFrom":subQ0}),-1.0]])]});}
            var Q51;
            Q51=makeQuery(id+"F0.imprint","IMPRINT",FACE,{"disambiguationData":[TD([[makeQuery(id+"F0.imprint","IMPRINT",EDGE,{"derivedFrom":sQuery(id+"F0.wireOp",EDGE,"E204.MirrorCS")}),-1.0]])]});
            var Q52;
            Q52=makeQuery(id+"F0.imprint","IMPRINT",FACE,{"disambiguationData":[TD([[makeQuery(id+"F0.imprint","IMPRINT",EDGE,{"derivedFrom":sQuery(id+"F0.wireOp",EDGE,"E149")}),-1.0]])]});
            var Q53;
            Q53=makeQuery(id+"F0.imprint","IMPRINT",FACE,{"disambiguationData":[TD([[makeQuery(id+"F0.imprint","IMPRINT",EDGE,{"derivedFrom":sQuery(id+"F0.wireOp",EDGE,"E168.MirrorCS")}),1.0]])]});
            var Q54;
            Q54=makeQuery(id+"F0.imprint","IMPRINT",FACE,{"disambiguationData":[TD([[makeQuery(id+"F0.imprint","IMPRINT",EDGE,{"derivedFrom":sQuery(id+"F0.wireOp",EDGE,"E85")}),-1.0]])]});
            var Q55;
            Q55=makeQuery(id+"F0.imprint","IMPRINT",FACE,{"disambiguationData":[TD([[makeQuery(id+"F0.imprint","IMPRINT",EDGE,{"derivedFrom":sQuery(id+"F0.wireOp",EDGE,"E53")}),-1.0]])]});
            var Q56;
            {var subQ0=sQuery(id+"F0.wireOp",EDGE,"E309.MirrorCS");var subQ1=sQuery(id+"F0.wireOp",EDGE,"E0");var subQ3=makeQuery(id+"F0.imprint","INTERSECT",VERTEX,{"derivedFrom":[subQ1,subQ0]});Q56=makeQuery(id+"F0.imprint","IMPRINT",FACE,{"disambiguationData":[TD([[makeQuery(id+"F0.imprint","IMPRINT",EDGE,{"disambiguationData":[TD([[subQ3,-1.0]])],"derivedFrom":subQ1}),1.0]])]});}
            var Q57;
            {var subQ0=sQuery(id+"F0.wireOp",EDGE,"E259.MirrorCS");Q57=makeQuery(id+"F0.imprint","IMPRINT",FACE,{"disambiguationData":[TD([[makeQuery(id+"F0.imprint","IMPRINT",EDGE,{"derivedFrom":subQ0}),-1.0]])]});}
            var Q58;
            Q58=makeQuery(id+"F0.imprint","IMPRINT",FACE,{"disambiguationData":[TD([[makeQuery(id+"F0.imprint","IMPRINT",EDGE,{"derivedFrom":sQuery(id+"F0.wireOp",EDGE,"E165.MirrorCS")}),1.0]])]});
            var Q59;
            {var subQ0=sQuery(id+"F0.wireOp",EDGE,"E60.filletArc");var subQ1=sQuery(id+"F0.wireOp",EDGE,"E0");var subQ3=makeQuery(id+"F0.imprint","INTERSECT",VERTEX,{"derivedFrom":[subQ1,subQ0]});Q59=makeQuery(id+"F0.imprint","IMPRINT",FACE,{"disambiguationData":[TD([[makeQuery(id+"F0.imprint","IMPRINT",EDGE,{"disambiguationData":[TD([[subQ3,1.0]])],"derivedFrom":subQ1}),1.0]])]});}
            var Q60;
            {var subQ0=sQuery(id+"F0.wireOp",EDGE,"E278.MirrorCS");var subQ1=sQuery(id+"F0.wireOp",EDGE,"E0");var subQ3=makeQuery(id+"F0.imprint","INTERSECT",VERTEX,{"derivedFrom":[subQ1,subQ0]});Q60=makeQuery(id+"F0.imprint","IMPRINT",FACE,{"disambiguationData":[TD([[makeQuery(id+"F0.imprint","IMPRINT",EDGE,{"disambiguationData":[TD([[subQ3,1.0]])],"derivedFrom":subQ1}),1.0]])]});}
            var Q61;
            {var subQ0=sQuery(id+"F0.wireOp",EDGE,"E120");Q61=makeQuery(id+"F0.imprint","IMPRINT",FACE,{"disambiguationData":[TD([[makeQuery(id+"F0.imprint","IMPRINT",EDGE,{"derivedFrom":subQ0}),1.0]])]});}
            var Q62;
            {var subQ0=sQuery(id+"F0.wireOp",EDGE,"E152");Q62=makeQuery(id+"F0.imprint","IMPRINT",FACE,{"disambiguationData":[TD([[makeQuery(id+"F0.imprint","IMPRINT",EDGE,{"derivedFrom":subQ0}),1.0]])]});}
            var Q63;
            {var subQ0=sQuery(id+"F0.wireOp",EDGE,"E228.MirrorCS");Q63=makeQuery(id+"F0.imprint","IMPRINT",FACE,{"disambiguationData":[TD([[makeQuery(id+"F0.imprint","IMPRINT",EDGE,{"derivedFrom":subQ0}),-1.0]])]});}
            var Q64;
            {var subQ0=sQuery(id+"F0.wireOp",EDGE,"E16");Q64=makeQuery(id+"F0.imprint","IMPRINT",FACE,{"disambiguationData":[TD([[makeQuery(id+"F0.imprint","IMPRINT",EDGE,{"derivedFrom":subQ0}),1.0]])]});}
            var Q65;
            {var subQ0=sQuery(id+"F0.wireOp",EDGE,"E245.MirrorCS");var subQ1=sQuery(id+"F0.wireOp",EDGE,"E0");var subQ3=makeQuery(id+"F0.imprint","INTERSECT",VERTEX,{"derivedFrom":[subQ1,subQ0]});Q65=makeQuery(id+"F0.imprint","IMPRINT",FACE,{"disambiguationData":[TD([[makeQuery(id+"F0.imprint","IMPRINT",EDGE,{"disambiguationData":[TD([[subQ3,-1.0]])],"derivedFrom":subQ1}),1.0]])]});}
            var Q66;
            {var subQ0=sQuery(id+"F0.wireOp",EDGE,"E225.MirrorCS");Q66=makeQuery(id+"F0.imprint","IMPRINT",FACE,{"disambiguationData":[TD([[makeQuery(id+"F0.imprint","IMPRINT",EDGE,{"derivedFrom":subQ0}),-1.0]])]});}
            var Q67;
            {var subQ0=sQuery(id+"F0.wireOp",EDGE,"E316.MirrorCS");var subQ1=sQuery(id+"F0.wireOp",EDGE,"E0");var subQ3=makeQuery(id+"F0.imprint","INTERSECT",VERTEX,{"derivedFrom":[subQ1,subQ0]});Q67=makeQuery(id+"F0.imprint","IMPRINT",FACE,{"disambiguationData":[TD([[makeQuery(id+"F0.imprint","IMPRINT",EDGE,{"disambiguationData":[TD([[subQ3,-1.0]])],"derivedFrom":subQ1}),1.0]])]});}
            var Q68;
            {var subQ0=sQuery(id+"F0.wireOp",EDGE,"E311.MirrorCS");var subQ1=sQuery(id+"F0.wireOp",EDGE,"E0");var subQ3=makeQuery(id+"F0.imprint","INTERSECT",VERTEX,{"derivedFrom":[subQ1,subQ0]});Q68=makeQuery(id+"F0.imprint","IMPRINT",FACE,{"disambiguationData":[TD([[makeQuery(id+"F0.imprint","IMPRINT",EDGE,{"disambiguationData":[TD([[subQ3,-1.0]])],"derivedFrom":subQ1}),1.0]])]});}
            var Q69;
            {var subQ0=sQuery(id+"F0.wireOp",EDGE,"E88");Q69=makeQuery(id+"F0.imprint","IMPRINT",FACE,{"disambiguationData":[TD([[makeQuery(id+"F0.imprint","IMPRINT",EDGE,{"derivedFrom":subQ0}),1.0]])]});}
            var Q70;
            {var subQ0=sQuery(id+"F0.wireOp",EDGE,"E112");Q70=makeQuery(id+"F0.imprint","IMPRINT",FACE,{"disambiguationData":[TD([[makeQuery(id+"F0.imprint","IMPRINT",EDGE,{"derivedFrom":subQ0}),1.0]])]});}
            var Q71;
            {var subQ0=sQuery(id+"F0.wireOp",EDGE,"E144");var subQ1=sQuery(id+"F0.wireOp",EDGE,"E0");var subQ3=makeQuery(id+"F0.imprint","INTERSECT",VERTEX,{"derivedFrom":[subQ1,subQ0]});Q71=makeQuery(id+"F0.imprint","IMPRINT",FACE,{"disambiguationData":[TD([[makeQuery(id+"F0.imprint","IMPRINT",EDGE,{"disambiguationData":[TD([[subQ3,-1.0]])],"derivedFrom":subQ1}),1.0]])]});}
            var Q72;
            {var subQ0=sQuery(id+"F0.wireOp",EDGE,"E260.MirrorCS");Q72=makeQuery(id+"F0.imprint","IMPRINT",FACE,{"disambiguationData":[TD([[makeQuery(id+"F0.imprint","IMPRINT",EDGE,{"derivedFrom":subQ0}),-1.0]])]});}
            var Q73;
            {var subQ0=sQuery(id+"F0.wireOp",EDGE,"E271.MirrorCS");Q73=makeQuery(id+"F0.imprint","IMPRINT",FACE,{"disambiguationData":[TD([[makeQuery(id+"F0.imprint","IMPRINT",EDGE,{"derivedFrom":subQ0}),-1.0]])]});}
            var Q74;
            {var subQ0=sQuery(id+"F0.wireOp",EDGE,"E8");Q74=makeQuery(id+"F0.imprint","IMPRINT",FACE,{"disambiguationData":[TD([[makeQuery(id+"F0.imprint","IMPRINT",EDGE,{"derivedFrom":subQ0}),1.0]])]});}
            extrude(context, id + "F1", {"entities" : qUnion([Q0, Q1, Q2, Q3, Q4, Q5, Q6, Q7, Q8, Q9, Q10, Q11, Q12, Q13, Q14, Q15, Q16, Q17, Q18, Q19, Q20, Q21, Q22, Q23, Q24, Q25, Q26, Q27, Q28, Q29, Q30, Q31, Q32, Q33, Q34, Q35, Q36, Q37, Q38, Q39, Q40, Q41, Q42, Q43, Q44, Q45, Q46, Q47, Q48, Q49, Q50, Q51, Q52, Q53, Q54, Q55, Q56, Q57, Q58, Q59, Q60, Q61, Q62, Q63, Q64, Q65, Q66, Q67, Q68, Q69, Q70, Q71, Q72, Q73, Q74]), "depth" : 12.7 * mm});
        }
        {
            var Q0;
            Q0=qCreatedBy(makeId("Front.planeOp"),FACE);
            var sketch = newSketch(context, id + "F2", { "sketchPlane" : qUnion([Q0])});
            skCircle(sketch, "E485", {"center": v(202.64, -38.91) * mm, "radius": 76.2 * mm});
            skCircle(sketch, "E486", {"center": v(202.64, -38.91) * mm, "radius": 6.35 * mm});
            skLineSegment(sketch, "E487", {"start": v(216.98, 48.42) * mm, "end": v(218.05, 48.13) * mm});
            skLineSegment(sketch, "E488", {"start": v(220.3, 45.26) * mm, "end": v(220.49, 38.5) * mm});
            skLineSegment(sketch, "E489", {"start": v(213.56, 47) * mm, "end": v(210.17, 41.19) * mm});
            skLineSegment(sketch, "E490", {"start": v(212.01, 36.7) * mm, "end": v(216.65, 35.47) * mm});
            skArc(sketch, "E491.filletArc", {"start": v(220.3, 45.26) * mm, "mid": v(219.66, 47.07) * mm, "end": v(218.05, 48.13) * mm});
            skArc(sketch, "E492.filletArc", {"start": v(216.98, 48.42) * mm, "mid": v(215.03, 48.29) * mm, "end": v(213.56, 47) * mm});
            skArc(sketch, "E493.filletArc", {"start": v(216.65, 35.47) * mm, "mid": v(219.33, 36.02) * mm, "end": v(220.49, 38.5) * mm});
            skArc(sketch, "E494.filletArc", {"start": v(210.17, 41.19) * mm, "mid": v(209.98, 38.5) * mm, "end": v(212.01, 36.7) * mm});
            skLineSegment(sketch, "E495", {"start": v(248.32, 37.16) * mm, "end": v(249.26, 36.57) * mm});
            skLineSegment(sketch, "E496", {"start": v(250.58, 33.17) * mm, "end": v(248.77, 26.64) * mm});
            skLineSegment(sketch, "E497", {"start": v(244.63, 36.81) * mm, "end": v(239.69, 32.24) * mm});
            skLineSegment(sketch, "E498", {"start": v(240.14, 27.42) * mm, "end": v(244.22, 24.87) * mm});
            skArc(sketch, "E499.filletArc", {"start": v(250.58, 33.17) * mm, "mid": v(250.48, 35.1) * mm, "end": v(249.26, 36.57) * mm});
            skArc(sketch, "E500.filletArc", {"start": v(248.32, 37.16) * mm, "mid": v(246.42, 37.61) * mm, "end": v(244.63, 36.81) * mm});
            skArc(sketch, "E501.filletArc", {"start": v(244.22, 24.87) * mm, "mid": v(246.94, 24.62) * mm, "end": v(248.77, 26.64) * mm});
            skArc(sketch, "E502.filletArc", {"start": v(239.69, 32.24) * mm, "mid": v(238.72, 29.72) * mm, "end": v(240.14, 27.42) * mm});
            skLineSegment(sketch, "E503", {"start": v(268.85, 20.14) * mm, "end": v(269.57, 19.3) * mm});
            skLineSegment(sketch, "E504", {"start": v(269.81, 15.66) * mm, "end": v(266.12, 9.98) * mm});
            skLineSegment(sketch, "E505", {"start": v(265.24, 20.92) * mm, "end": v(259.15, 18.05) * mm});
            skLineSegment(sketch, "E506", {"start": v(258.13, 13.31) * mm, "end": v(261.25, 9.66) * mm});
            skArc(sketch, "E507.filletArc", {"start": v(269.81, 15.66) * mm, "mid": v(270.3, 17.52) * mm, "end": v(269.57, 19.3) * mm});
            skArc(sketch, "E508.filletArc", {"start": v(268.85, 20.14) * mm, "mid": v(267.18, 21.14) * mm, "end": v(265.24, 20.92) * mm});
            skArc(sketch, "E509.filletArc", {"start": v(261.25, 9.66) * mm, "mid": v(263.76, 8.6) * mm, "end": v(266.12, 9.98) * mm});
            skArc(sketch, "E510.filletArc", {"start": v(259.15, 18.05) * mm, "mid": v(257.47, 15.93) * mm, "end": v(258.13, 13.31) * mm});
            skLineSegment(sketch, "E511", {"start": v(284.23, -4.25) * mm, "end": v(284.6, -5.3) * mm});
            skLineSegment(sketch, "E512", {"start": v(283.55, -8.79) * mm, "end": v(278.1, -12.82) * mm});
            skLineSegment(sketch, "E513", {"start": v(281.1, -2.26) * mm, "end": v(274.4, -2.82) * mm});
            skLineSegment(sketch, "E514", {"start": v(271.79, -6.9) * mm, "end": v(273.43, -11.41) * mm});
            skArc(sketch, "E515.filletArc", {"start": v(283.55, -8.79) * mm, "mid": v(284.66, -7.22) * mm, "end": v(284.6, -5.3) * mm});
            skArc(sketch, "E516.filletArc", {"start": v(284.23, -4.25) * mm, "mid": v(283, -2.73) * mm, "end": v(281.1, -2.26) * mm});
            skArc(sketch, "E517.filletArc", {"start": v(273.43, -11.41) * mm, "mid": v(275.42, -13.29) * mm, "end": v(278.1, -12.82) * mm});
            skArc(sketch, "E518.filletArc", {"start": v(274.4, -2.82) * mm, "mid": v(272.08, -4.21) * mm, "end": v(271.79, -6.9) * mm});
            skLineSegment(sketch, "E519", {"start": v(289.45, -21.92) * mm, "end": v(289.73, -23) * mm});
            skLineSegment(sketch, "E520", {"start": v(288.38, -26.38) * mm, "end": v(282.6, -29.92) * mm});
            skLineSegment(sketch, "E521", {"start": v(286.52, -19.66) * mm, "end": v(279.78, -19.64) * mm});
            skLineSegment(sketch, "E522", {"start": v(276.83, -23.47) * mm, "end": v(278.07, -28.12) * mm});
            skArc(sketch, "E523.filletArc", {"start": v(288.38, -26.38) * mm, "mid": v(289.62, -24.91) * mm, "end": v(289.73, -23) * mm});
            skArc(sketch, "E524.filletArc", {"start": v(289.45, -21.92) * mm, "mid": v(288.36, -20.3) * mm, "end": v(286.52, -19.66) * mm});
            skArc(sketch, "E525.filletArc", {"start": v(278.07, -28.12) * mm, "mid": v(279.88, -30.16) * mm, "end": v(282.6, -29.92) * mm});
            skArc(sketch, "E526.filletArc", {"start": v(279.78, -19.64) * mm, "mid": v(277.36, -20.83) * mm, "end": v(276.83, -23.47) * mm});
            skLineSegment(sketch, "E527.MirrorCS", {"start": v(184.8, 47.47) * mm, "end": v(183.73, 47.19) * mm});
            skLineSegment(sketch, "E528.MirrorCS", {"start": v(156.96, 37.16) * mm, "end": v(156.02, 36.57) * mm});
            skLineSegment(sketch, "E529.MirrorCS", {"start": v(121.05, -4.25) * mm, "end": v(120.67, -5.3) * mm});
            skArc(sketch, "E530.MirrorCS", {"start": v(184.8, 47.47) * mm, "mid": v(186.75, 47.35) * mm, "end": v(188.22, 46.06) * mm});
            skArc(sketch, "E531.MirrorCS", {"start": v(181.47, 44.32) * mm, "mid": v(182.12, 46.13) * mm, "end": v(183.73, 47.19) * mm});
            skArc(sketch, "E532.MirrorCS", {"start": v(135.46, 15.66) * mm, "mid": v(134.98, 17.52) * mm, "end": v(135.7, 19.3) * mm});
            skArc(sketch, "E533.MirrorCS", {"start": v(117.55, -29.04) * mm, "mid": v(116.07, -27.81) * mm, "end": v(115.63, -25.94) * mm});
            skLineSegment(sketch, "E534.MirrorCS", {"start": v(136.42, 20.14) * mm, "end": v(135.7, 19.3) * mm});
            skLineSegment(sketch, "E535.MirrorCS", {"start": v(115.72, -24.84) * mm, "end": v(115.63, -25.94) * mm});
            skArc(sketch, "E536.MirrorCS", {"start": v(161.06, 24.87) * mm, "mid": v(158.34, 24.62) * mm, "end": v(156.5, 26.64) * mm});
            skArc(sketch, "E537.MirrorCS", {"start": v(156.96, 37.16) * mm, "mid": v(158.86, 37.61) * mm, "end": v(160.65, 36.81) * mm});
            skArc(sketch, "E538.MirrorCS", {"start": v(121.72, -8.79) * mm, "mid": v(120.62, -7.22) * mm, "end": v(120.67, -5.3) * mm});
            skArc(sketch, "E539.MirrorCS", {"start": v(154.7, 33.17) * mm, "mid": v(154.8, 35.1) * mm, "end": v(156.02, 36.57) * mm});
            skArc(sketch, "E540.MirrorCS", {"start": v(191.61, 40.25) * mm, "mid": v(191.8, 37.55) * mm, "end": v(189.77, 35.77) * mm});
            skArc(sketch, "E541.MirrorCS", {"start": v(146.13, 18.05) * mm, "mid": v(147.81, 15.93) * mm, "end": v(147.15, 13.31) * mm});
            skArc(sketch, "E542.MirrorCS", {"start": v(124.84, -20.9) * mm, "mid": v(127.44, -21.66) * mm, "end": v(128.42, -24.17) * mm});
            skArc(sketch, "E543.MirrorCS", {"start": v(185.13, 34.52) * mm, "mid": v(182.45, 35.08) * mm, "end": v(181.29, 37.55) * mm});
            skArc(sketch, "E544.MirrorCS", {"start": v(144.03, 9.66) * mm, "mid": v(141.51, 8.6) * mm, "end": v(139.16, 9.98) * mm});
            skArc(sketch, "E545.MirrorCS", {"start": v(128, -28.96) * mm, "mid": v(126.57, -31.29) * mm, "end": v(123.85, -31.53) * mm});
            skArc(sketch, "E546.MirrorCS", {"start": v(136.42, 20.14) * mm, "mid": v(138.1, 21.14) * mm, "end": v(140.04, 20.92) * mm});
            skArc(sketch, "E547.MirrorCS", {"start": v(115.72, -24.84) * mm, "mid": v(116.5, -23.05) * mm, "end": v(118.22, -22.1) * mm});
            skLineSegment(sketch, "E548.MirrorCS", {"start": v(189.77, 35.77) * mm, "end": v(185.13, 34.52) * mm});
            skLineSegment(sketch, "E549.MirrorCS", {"start": v(147.15, 13.31) * mm, "end": v(144.03, 9.66) * mm});
            skLineSegment(sketch, "E550.MirrorCS", {"start": v(128.42, -24.17) * mm, "end": v(128, -28.96) * mm});
            skLineSegment(sketch, "E551.MirrorCS", {"start": v(118.22, -22.1) * mm, "end": v(124.84, -20.9) * mm});
            skLineSegment(sketch, "E552.MirrorCS", {"start": v(188.22, 46.06) * mm, "end": v(191.61, 40.25) * mm});
            skLineSegment(sketch, "E553.MirrorCS", {"start": v(140.04, 20.92) * mm, "end": v(146.13, 18.05) * mm});
            skLineSegment(sketch, "E554.MirrorCS", {"start": v(117.55, -29.04) * mm, "end": v(123.85, -31.53) * mm});
            skLineSegment(sketch, "E555.MirrorCS", {"start": v(181.47, 44.32) * mm, "end": v(181.29, 37.55) * mm});
            skLineSegment(sketch, "E556.MirrorCS", {"start": v(135.46, 15.66) * mm, "end": v(139.16, 9.98) * mm});
            skArc(sketch, "E557.MirrorCS", {"start": v(130.88, -2.82) * mm, "mid": v(133.2, -4.21) * mm, "end": v(133.49, -6.9) * mm});
            skArc(sketch, "E558.MirrorCS", {"start": v(165.59, 32.24) * mm, "mid": v(166.55, 29.72) * mm, "end": v(165.13, 27.42) * mm});
            skArc(sketch, "E559.MirrorCS", {"start": v(131.85, -11.41) * mm, "mid": v(129.86, -13.29) * mm, "end": v(127.17, -12.82) * mm});
            skArc(sketch, "E560.MirrorCS", {"start": v(121.05, -4.25) * mm, "mid": v(122.27, -2.73) * mm, "end": v(124.17, -2.26) * mm});
            skLineSegment(sketch, "E561.MirrorCS", {"start": v(133.49, -6.9) * mm, "end": v(131.85, -11.41) * mm});
            skLineSegment(sketch, "E562.MirrorCS", {"start": v(165.13, 27.42) * mm, "end": v(161.06, 24.87) * mm});
            skLineSegment(sketch, "E563.MirrorCS", {"start": v(124.17, -2.26) * mm, "end": v(130.88, -2.82) * mm});
            skLineSegment(sketch, "E564.MirrorCS", {"start": v(160.65, 36.81) * mm, "end": v(165.59, 32.24) * mm});
            skLineSegment(sketch, "E565.MirrorCS", {"start": v(154.7, 33.17) * mm, "end": v(156.5, 26.64) * mm});
            skLineSegment(sketch, "E566.MirrorCS", {"start": v(121.72, -8.79) * mm, "end": v(127.17, -12.82) * mm});
            skLineSegment(sketch, "E567.MirrorCS", {"start": v(268.85, -97.96) * mm, "end": v(269.57, -97.12) * mm});
            skLineSegment(sketch, "E568.MirrorCS", {"start": v(216.98, -126.24) * mm, "end": v(218.05, -125.95) * mm});
            skArc(sketch, "E569.MirrorCS", {"start": v(269.81, -93.48) * mm, "mid": v(270.3, -95.34) * mm, "end": v(269.57, -97.12) * mm});
            skLineSegment(sketch, "E570.MirrorCS", {"start": v(156.96, -114.98) * mm, "end": v(156.02, -114.4) * mm});
            skLineSegment(sketch, "E571.MirrorCS", {"start": v(290.77, -49.04) * mm, "end": v(290.86, -47.94) * mm});
            skArc(sketch, "E572.MirrorCS", {"start": v(156.96, -114.98) * mm, "mid": v(158.86, -115.43) * mm, "end": v(160.65, -114.64) * mm});
            skArc(sketch, "E573.MirrorCS", {"start": v(154.7, -111) * mm, "mid": v(154.8, -112.92) * mm, "end": v(156.02, -114.4) * mm});
            skArc(sketch, "E574.MirrorCS", {"start": v(288.95, -44.84) * mm, "mid": v(290.42, -46.07) * mm, "end": v(290.86, -47.94) * mm});
            skArc(sketch, "E575.MirrorCS", {"start": v(220.3, -123.09) * mm, "mid": v(219.66, -124.9) * mm, "end": v(218.05, -125.95) * mm});
            skArc(sketch, "E576.MirrorCS", {"start": v(290.77, -49.04) * mm, "mid": v(289.98, -50.83) * mm, "end": v(288.27, -51.78) * mm});
            skArc(sketch, "E577.MirrorCS", {"start": v(268.85, -97.96) * mm, "mid": v(267.18, -98.97) * mm, "end": v(265.24, -98.74) * mm});
            skArc(sketch, "E578.MirrorCS", {"start": v(216.98, -126.24) * mm, "mid": v(215.03, -126.11) * mm, "end": v(213.56, -124.83) * mm});
            skLineSegment(sketch, "E579.MirrorCS", {"start": v(284.23, -73.57) * mm, "end": v(284.6, -72.53) * mm});
            skLineSegment(sketch, "E580.MirrorCS", {"start": v(248.32, -114.98) * mm, "end": v(249.26, -114.4) * mm});
            skArc(sketch, "E581.MirrorCS", {"start": v(250.58, -111) * mm, "mid": v(250.48, -112.92) * mm, "end": v(249.26, -114.4) * mm});
            skLineSegment(sketch, "E582.MirrorCS", {"start": v(117, -51.78) * mm, "end": v(123.63, -52.97) * mm});
            skLineSegment(sketch, "E583.MirrorCS", {"start": v(114.5, -49.04) * mm, "end": v(114.41, -47.94) * mm});
            skLineSegment(sketch, "E584.MirrorCS", {"start": v(269.81, -93.48) * mm, "end": v(266.12, -87.8) * mm});
            skLineSegment(sketch, "E585.MirrorCS", {"start": v(220.3, -123.09) * mm, "end": v(220.49, -116.31) * mm});
            skLineSegment(sketch, "E586.MirrorCS", {"start": v(188.22, -123.89) * mm, "end": v(191.61, -118.07) * mm});
            skArc(sketch, "E587.MirrorCS", {"start": v(161.06, -102.7) * mm, "mid": v(158.34, -102.44) * mm, "end": v(156.5, -104.47) * mm});
            skLineSegment(sketch, "E588.MirrorCS", {"start": v(288.95, -44.84) * mm, "end": v(282.64, -42.35) * mm});
            skLineSegment(sketch, "E589.MirrorCS", {"start": v(244.63, -114.64) * mm, "end": v(239.69, -110.07) * mm});
            skLineSegment(sketch, "E590.MirrorCS", {"start": v(265.24, -98.74) * mm, "end": v(259.15, -95.87) * mm});
            skLineSegment(sketch, "E591.MirrorCS", {"start": v(213.56, -124.83) * mm, "end": v(210.17, -119.01) * mm});
            skLineSegment(sketch, "E592.MirrorCS", {"start": v(140.04, -98.74) * mm, "end": v(146.13, -95.87) * mm});
            skLineSegment(sketch, "E593.MirrorCS", {"start": v(288.27, -51.78) * mm, "end": v(281.65, -52.97) * mm});
            skLineSegment(sketch, "E594.MirrorCS", {"start": v(133.49, -70.92) * mm, "end": v(131.85, -66.41) * mm});
            skArc(sketch, "E595.MirrorCS", {"start": v(121.72, -69.04) * mm, "mid": v(120.62, -70.6) * mm, "end": v(120.67, -72.53) * mm});
            skLineSegment(sketch, "E596.MirrorCS", {"start": v(278.07, -49.7) * mm, "end": v(278.49, -44.92) * mm});
            skLineSegment(sketch, "E597.MirrorCS", {"start": v(258.13, -91.14) * mm, "end": v(261.25, -87.48) * mm});
            skLineSegment(sketch, "E598.MirrorCS", {"start": v(212.01, -114.53) * mm, "end": v(216.65, -113.29) * mm});
            skLineSegment(sketch, "E599.MirrorCS", {"start": v(116.33, -44.84) * mm, "end": v(122.63, -42.35) * mm});
            skArc(sketch, "E600.MirrorCS", {"start": v(126.79, -44.92) * mm, "mid": v(125.36, -42.6) * mm, "end": v(122.63, -42.35) * mm});
            skLineSegment(sketch, "E601.MirrorCS", {"start": v(121.05, -73.57) * mm, "end": v(120.67, -72.53) * mm});
            skLineSegment(sketch, "E602.MirrorCS", {"start": v(281.1, -75.56) * mm, "end": v(274.4, -75) * mm});
            skLineSegment(sketch, "E603.MirrorCS", {"start": v(181.47, -122.15) * mm, "end": v(181.29, -115.37) * mm});
            skArc(sketch, "E604.MirrorCS", {"start": v(191.61, -118.07) * mm, "mid": v(191.8, -115.37) * mm, "end": v(189.77, -113.6) * mm});
            skLineSegment(sketch, "E605.MirrorCS", {"start": v(135.46, -93.48) * mm, "end": v(139.16, -87.8) * mm});
            skArc(sketch, "E606.MirrorCS", {"start": v(146.13, -95.87) * mm, "mid": v(147.81, -93.75) * mm, "end": v(147.15, -91.14) * mm});
            skArc(sketch, "E607.MirrorCS", {"start": v(278.49, -44.92) * mm, "mid": v(279.92, -42.6) * mm, "end": v(282.64, -42.35) * mm});
            skArc(sketch, "E608.MirrorCS", {"start": v(261.25, -87.48) * mm, "mid": v(263.76, -86.42) * mm, "end": v(266.12, -87.8) * mm});
            skArc(sketch, "E609.MirrorCS", {"start": v(216.65, -113.29) * mm, "mid": v(219.33, -113.84) * mm, "end": v(220.49, -116.31) * mm});
            skArc(sketch, "E610.MirrorCS", {"start": v(130.88, -75) * mm, "mid": v(133.2, -73.6) * mm, "end": v(133.49, -70.92) * mm});
            skArc(sketch, "E611.MirrorCS", {"start": v(123.63, -52.97) * mm, "mid": v(126.23, -52.23) * mm, "end": v(127.2, -49.7) * mm});
            skArc(sketch, "E612.MirrorCS", {"start": v(281.65, -52.97) * mm, "mid": v(279.05, -52.23) * mm, "end": v(278.07, -49.7) * mm});
            skArc(sketch, "E613.MirrorCS", {"start": v(259.15, -95.87) * mm, "mid": v(257.47, -93.75) * mm, "end": v(258.13, -91.14) * mm});
            skArc(sketch, "E614.MirrorCS", {"start": v(210.17, -119.01) * mm, "mid": v(209.98, -116.32) * mm, "end": v(212.01, -114.53) * mm});
            skArc(sketch, "E615.MirrorCS", {"start": v(165.59, -110.07) * mm, "mid": v(166.55, -107.54) * mm, "end": v(165.13, -105.24) * mm});
            skArc(sketch, "E616.MirrorCS", {"start": v(185.13, -112.35) * mm, "mid": v(182.45, -112.9) * mm, "end": v(181.29, -115.37) * mm});
            skArc(sketch, "E617.MirrorCS", {"start": v(239.69, -110.07) * mm, "mid": v(238.72, -107.54) * mm, "end": v(240.14, -105.24) * mm});
            skLineSegment(sketch, "E618.MirrorCS", {"start": v(184.8, -125.3) * mm, "end": v(183.73, -125) * mm});
            skArc(sketch, "E619.MirrorCS", {"start": v(131.85, -66.41) * mm, "mid": v(129.86, -64.53) * mm, "end": v(127.17, -65) * mm});
            skLineSegment(sketch, "E620.MirrorCS", {"start": v(121.72, -69.04) * mm, "end": v(127.17, -65) * mm});
            skLineSegment(sketch, "E621.MirrorCS", {"start": v(127.2, -49.7) * mm, "end": v(126.79, -44.92) * mm});
            skLineSegment(sketch, "E622.MirrorCS", {"start": v(136.42, -97.96) * mm, "end": v(135.7, -97.12) * mm});
            skArc(sketch, "E623.MirrorCS", {"start": v(274.4, -75) * mm, "mid": v(272.08, -73.6) * mm, "end": v(271.79, -70.92) * mm});
            skArc(sketch, "E624.MirrorCS", {"start": v(284.23, -73.57) * mm, "mid": v(283, -75.1) * mm, "end": v(281.1, -75.56) * mm});
            skArc(sketch, "E625.MirrorCS", {"start": v(184.8, -125.3) * mm, "mid": v(186.75, -125.17) * mm, "end": v(188.22, -123.89) * mm});
            skArc(sketch, "E626.MirrorCS", {"start": v(136.42, -97.96) * mm, "mid": v(138.1, -98.97) * mm, "end": v(140.04, -98.74) * mm});
            skLineSegment(sketch, "E627.MirrorCS", {"start": v(165.13, -105.24) * mm, "end": v(161.06, -102.7) * mm});
            skLineSegment(sketch, "E628.MirrorCS", {"start": v(271.79, -70.92) * mm, "end": v(273.43, -66.41) * mm});
            skLineSegment(sketch, "E629.MirrorCS", {"start": v(240.14, -105.24) * mm, "end": v(244.22, -102.7) * mm});
            skArc(sketch, "E630.MirrorCS", {"start": v(244.22, -102.7) * mm, "mid": v(246.94, -102.44) * mm, "end": v(248.77, -104.47) * mm});
            skLineSegment(sketch, "E631.MirrorCS", {"start": v(154.7, -111) * mm, "end": v(156.5, -104.47) * mm});
            skArc(sketch, "E632.MirrorCS", {"start": v(273.43, -66.41) * mm, "mid": v(275.42, -64.53) * mm, "end": v(278.1, -65) * mm});
            skLineSegment(sketch, "E633.MirrorCS", {"start": v(147.15, -91.14) * mm, "end": v(144.03, -87.48) * mm});
            skArc(sketch, "E634.MirrorCS", {"start": v(116.33, -44.84) * mm, "mid": v(114.86, -46.07) * mm, "end": v(114.41, -47.94) * mm});
            skLineSegment(sketch, "E635.MirrorCS", {"start": v(250.58, -111) * mm, "end": v(248.77, -104.47) * mm});
            skLineSegment(sketch, "E636.MirrorCS", {"start": v(189.77, -113.6) * mm, "end": v(185.13, -112.35) * mm});
            skArc(sketch, "E637.MirrorCS", {"start": v(135.46, -93.48) * mm, "mid": v(134.98, -95.34) * mm, "end": v(135.7, -97.12) * mm});
            skLineSegment(sketch, "E638.MirrorCS", {"start": v(160.65, -114.64) * mm, "end": v(165.59, -110.07) * mm});
            skArc(sketch, "E639.MirrorCS", {"start": v(121.05, -73.57) * mm, "mid": v(122.27, -75.1) * mm, "end": v(124.17, -75.56) * mm});
            skArc(sketch, "E640.MirrorCS", {"start": v(144.03, -87.48) * mm, "mid": v(141.51, -86.42) * mm, "end": v(139.16, -87.8) * mm});
            skLineSegment(sketch, "E641.MirrorCS", {"start": v(283.55, -69.04) * mm, "end": v(278.1, -65) * mm});
            skArc(sketch, "E642.MirrorCS", {"start": v(283.55, -69.04) * mm, "mid": v(284.66, -70.6) * mm, "end": v(284.6, -72.53) * mm});
            skArc(sketch, "E643.MirrorCS", {"start": v(114.5, -49.04) * mm, "mid": v(115.3, -50.83) * mm, "end": v(117, -51.78) * mm});
            skArc(sketch, "E644.MirrorCS", {"start": v(181.47, -122.15) * mm, "mid": v(182.12, -123.95) * mm, "end": v(183.73, -125) * mm});
            skLineSegment(sketch, "E645.MirrorCS", {"start": v(124.17, -75.56) * mm, "end": v(130.88, -75) * mm});
            skArc(sketch, "E646.MirrorCS", {"start": v(248.32, -114.98) * mm, "mid": v(246.42, -115.43) * mm, "end": v(244.63, -114.64) * mm});
            skSolve(sketch);
        }
        {
            var Q0;
            Q0=makeQuery(id+"F2.imprint","IMPRINT",FACE,{"disambiguationData":[TD([[makeQuery(id+"F2.imprint","IMPRINT",EDGE,{"derivedFrom":sQuery(id+"F2.wireOp",EDGE,"E486")}),-1.0]])]});
            var Q1;
            Q1=makeQuery(id+"F2.imprint","IMPRINT",FACE,{"disambiguationData":[TD([[makeQuery(id+"F2.imprint","IMPRINT",EDGE,{"derivedFrom":sQuery(id+"F2.wireOp",EDGE,"E532.MirrorCS")}),-1.0]])]});
            var Q2;
            Q2=makeQuery(id+"F2.imprint","IMPRINT",FACE,{"disambiguationData":[TD([[makeQuery(id+"F2.imprint","IMPRINT",EDGE,{"derivedFrom":sQuery(id+"F2.wireOp",EDGE,"E580.MirrorCS")}),1.0]])]});
            var Q3;
            Q3=makeQuery(id+"F2.imprint","IMPRINT",FACE,{"disambiguationData":[TD([[makeQuery(id+"F2.imprint","IMPRINT",EDGE,{"derivedFrom":sQuery(id+"F2.wireOp",EDGE,"E595.MirrorCS")}),1.0]])]});
            var Q4;
            {var subQ2=sQuery(id+"F2.wireOp",EDGE,"E586.MirrorCS");Q4=makeQuery(id+"F2.imprint","IMPRINT",FACE,{"disambiguationData":[TD([[makeQuery(id+"F2.imprint","IMPRINT",EDGE,{"derivedFrom":subQ2}),1.0]])]});}
            var Q5;
            Q5=makeQuery(id+"F2.imprint","IMPRINT",FACE,{"disambiguationData":[TD([[makeQuery(id+"F2.imprint","IMPRINT",EDGE,{"derivedFrom":sQuery(id+"F2.wireOp",EDGE,"E533.MirrorCS")}),-1.0]])]});
            var Q6;
            Q6=makeQuery(id+"F2.imprint","IMPRINT",FACE,{"disambiguationData":[TD([[makeQuery(id+"F2.imprint","IMPRINT",EDGE,{"derivedFrom":sQuery(id+"F2.wireOp",EDGE,"E592.MirrorCS")}),1.0]])]});
            var Q7;
            Q7=makeQuery(id+"F2.imprint","IMPRINT",FACE,{"disambiguationData":[TD([[makeQuery(id+"F2.imprint","IMPRINT",EDGE,{"derivedFrom":sQuery(id+"F2.wireOp",EDGE,"E495")}),-1.0]])]});
            var Q8;
            Q8=makeQuery(id+"F2.imprint","IMPRINT",FACE,{"disambiguationData":[TD([[makeQuery(id+"F2.imprint","IMPRINT",EDGE,{"derivedFrom":sQuery(id+"F2.wireOp",EDGE,"E582.MirrorCS")}),1.0]])]});
            var Q9;
            Q9=makeQuery(id+"F2.imprint","IMPRINT",FACE,{"disambiguationData":[TD([[makeQuery(id+"F2.imprint","IMPRINT",EDGE,{"derivedFrom":sQuery(id+"F2.wireOp",EDGE,"E527.MirrorCS")}),1.0]])]});
            var Q10;
            Q10=makeQuery(id+"F2.imprint","IMPRINT",FACE,{"disambiguationData":[TD([[makeQuery(id+"F2.imprint","IMPRINT",EDGE,{"derivedFrom":sQuery(id+"F2.wireOp",EDGE,"E529.MirrorCS")}),1.0]])]});
            var Q11;
            Q11=makeQuery(id+"F2.imprint","IMPRINT",FACE,{"disambiguationData":[TD([[makeQuery(id+"F2.imprint","IMPRINT",EDGE,{"derivedFrom":sQuery(id+"F2.wireOp",EDGE,"E487")}),-1.0]])]});
            var Q12;
            Q12=makeQuery(id+"F2.imprint","IMPRINT",FACE,{"disambiguationData":[TD([[makeQuery(id+"F2.imprint","IMPRINT",EDGE,{"derivedFrom":sQuery(id+"F2.wireOp",EDGE,"E503")}),-1.0]])]});
            var Q13;
            Q13=makeQuery(id+"F2.imprint","IMPRINT",FACE,{"disambiguationData":[TD([[makeQuery(id+"F2.imprint","IMPRINT",EDGE,{"derivedFrom":sQuery(id+"F2.wireOp",EDGE,"E528.MirrorCS")}),1.0]])]});
            var Q14;
            Q14=makeQuery(id+"F2.imprint","IMPRINT",FACE,{"disambiguationData":[TD([[makeQuery(id+"F2.imprint","IMPRINT",EDGE,{"derivedFrom":sQuery(id+"F2.wireOp",EDGE,"E511")}),-1.0]])]});
            var Q15;
            Q15=makeQuery(id+"F2.imprint","IMPRINT",FACE,{"disambiguationData":[TD([[makeQuery(id+"F2.imprint","IMPRINT",EDGE,{"derivedFrom":sQuery(id+"F2.wireOp",EDGE,"E579.MirrorCS")}),1.0]])]});
            var Q16;
            Q16=makeQuery(id+"F2.imprint","IMPRINT",FACE,{"disambiguationData":[TD([[makeQuery(id+"F2.imprint","IMPRINT",EDGE,{"derivedFrom":sQuery(id+"F2.wireOp",EDGE,"E571.MirrorCS")}),1.0]])]});
            var Q17;
            Q17=makeQuery(id+"F2.imprint","IMPRINT",FACE,{"disambiguationData":[TD([[makeQuery(id+"F2.imprint","IMPRINT",EDGE,{"derivedFrom":sQuery(id+"F2.wireOp",EDGE,"E519")}),-1.0]])]});
            var Q18;
            Q18=makeQuery(id+"F2.imprint","IMPRINT",FACE,{"disambiguationData":[TD([[makeQuery(id+"F2.imprint","IMPRINT",EDGE,{"derivedFrom":sQuery(id+"F2.wireOp",EDGE,"E570.MirrorCS")}),-1.0]])]});
            var Q19;
            Q19=makeQuery(id+"F2.imprint","IMPRINT",FACE,{"disambiguationData":[TD([[makeQuery(id+"F2.imprint","IMPRINT",EDGE,{"derivedFrom":sQuery(id+"F2.wireOp",EDGE,"E568.MirrorCS")}),1.0]])]});
            var Q20;
            Q20=makeQuery(id+"F2.imprint","IMPRINT",FACE,{"disambiguationData":[TD([[makeQuery(id+"F2.imprint","IMPRINT",EDGE,{"derivedFrom":sQuery(id+"F2.wireOp",EDGE,"E567.MirrorCS")}),1.0]])]});
            var Q21;
            {var subQ0=sQuery(id+"F2.wireOp",EDGE,"E633.MirrorCS");Q21=makeQuery(id+"F2.imprint","IMPRINT",FACE,{"disambiguationData":[TD([[makeQuery(id+"F2.imprint","IMPRINT",EDGE,{"derivedFrom":subQ0}),1.0]])]});}
            var Q22;
            {var subQ0=sQuery(id+"F2.wireOp",EDGE,"E594.MirrorCS");Q22=makeQuery(id+"F2.imprint","IMPRINT",FACE,{"disambiguationData":[TD([[makeQuery(id+"F2.imprint","IMPRINT",EDGE,{"derivedFrom":subQ0}),1.0]])]});}
            var Q23;
            {var subQ0=sQuery(id+"F2.wireOp",EDGE,"E629.MirrorCS");Q23=makeQuery(id+"F2.imprint","IMPRINT",FACE,{"disambiguationData":[TD([[makeQuery(id+"F2.imprint","IMPRINT",EDGE,{"derivedFrom":subQ0}),-1.0]])]});}
            var Q24;
            {var subQ0=sQuery(id+"F2.wireOp",EDGE,"E498");Q24=makeQuery(id+"F2.imprint","IMPRINT",FACE,{"disambiguationData":[TD([[makeQuery(id+"F2.imprint","IMPRINT",EDGE,{"derivedFrom":subQ0}),1.0]])]});}
            var Q25;
            {var subQ0=sQuery(id+"F2.wireOp",EDGE,"E514");Q25=makeQuery(id+"F2.imprint","IMPRINT",FACE,{"disambiguationData":[TD([[makeQuery(id+"F2.imprint","IMPRINT",EDGE,{"derivedFrom":subQ0}),1.0]])]});}
            var Q26;
            {var subQ0=sQuery(id+"F2.wireOp",EDGE,"E562.MirrorCS");Q26=makeQuery(id+"F2.imprint","IMPRINT",FACE,{"disambiguationData":[TD([[makeQuery(id+"F2.imprint","IMPRINT",EDGE,{"derivedFrom":subQ0}),-1.0]])]});}
            var Q27;
            {var subQ0=sQuery(id+"F2.wireOp",EDGE,"E522");Q27=makeQuery(id+"F2.imprint","IMPRINT",FACE,{"disambiguationData":[TD([[makeQuery(id+"F2.imprint","IMPRINT",EDGE,{"derivedFrom":subQ0}),1.0]])]});}
            var Q28;
            {var subQ0=sQuery(id+"F2.wireOp",EDGE,"E596.MirrorCS");Q28=makeQuery(id+"F2.imprint","IMPRINT",FACE,{"disambiguationData":[TD([[makeQuery(id+"F2.imprint","IMPRINT",EDGE,{"derivedFrom":subQ0}),-1.0]])]});}
            var Q29;
            {var subQ5=sQuery(id+"F2.wireOp",EDGE,"E548.MirrorCS");Q29=makeQuery(id+"F2.imprint","IMPRINT",FACE,{"disambiguationData":[TD([[makeQuery(id+"F2.imprint","IMPRINT",EDGE,{"derivedFrom":subQ5}),-1.0]])]});}
            var Q30;
            {var subQ0=sQuery(id+"F2.wireOp",EDGE,"E621.MirrorCS");Q30=makeQuery(id+"F2.imprint","IMPRINT",FACE,{"disambiguationData":[TD([[makeQuery(id+"F2.imprint","IMPRINT",EDGE,{"derivedFrom":subQ0}),1.0]])]});}
            var Q31;
            {var subQ0=sQuery(id+"F2.wireOp",EDGE,"E628.MirrorCS");Q31=makeQuery(id+"F2.imprint","IMPRINT",FACE,{"disambiguationData":[TD([[makeQuery(id+"F2.imprint","IMPRINT",EDGE,{"derivedFrom":subQ0}),-1.0]])]});}
            var Q32;
            {var subQ0=sQuery(id+"F2.wireOp",EDGE,"E549.MirrorCS");Q32=makeQuery(id+"F2.imprint","IMPRINT",FACE,{"disambiguationData":[TD([[makeQuery(id+"F2.imprint","IMPRINT",EDGE,{"derivedFrom":subQ0}),-1.0]])]});}
            var Q33;
            {var subQ0=sQuery(id+"F2.wireOp",EDGE,"E490");Q33=makeQuery(id+"F2.imprint","IMPRINT",FACE,{"disambiguationData":[TD([[makeQuery(id+"F2.imprint","IMPRINT",EDGE,{"derivedFrom":subQ0}),1.0]])]});}
            var Q34;
            {var subQ0=sQuery(id+"F2.wireOp",EDGE,"E597.MirrorCS");Q34=makeQuery(id+"F2.imprint","IMPRINT",FACE,{"disambiguationData":[TD([[makeQuery(id+"F2.imprint","IMPRINT",EDGE,{"derivedFrom":subQ0}),-1.0]])]});}
            var Q35;
            {var subQ0=sQuery(id+"F2.wireOp",EDGE,"E550.MirrorCS");Q35=makeQuery(id+"F2.imprint","IMPRINT",FACE,{"disambiguationData":[TD([[makeQuery(id+"F2.imprint","IMPRINT",EDGE,{"derivedFrom":subQ0}),-1.0]])]});}
            var Q36;
            {var subQ0=sQuery(id+"F2.wireOp",EDGE,"E598.MirrorCS");Q36=makeQuery(id+"F2.imprint","IMPRINT",FACE,{"disambiguationData":[TD([[makeQuery(id+"F2.imprint","IMPRINT",EDGE,{"derivedFrom":subQ0}),-1.0]])]});}
            var Q37;
            {var subQ0=sQuery(id+"F2.wireOp",EDGE,"E627.MirrorCS");Q37=makeQuery(id+"F2.imprint","IMPRINT",FACE,{"disambiguationData":[TD([[makeQuery(id+"F2.imprint","IMPRINT",EDGE,{"derivedFrom":subQ0}),1.0]])]});}
            var Q38;
            {var subQ5=sQuery(id+"F2.wireOp",EDGE,"E636.MirrorCS");Q38=makeQuery(id+"F2.imprint","IMPRINT",FACE,{"disambiguationData":[TD([[makeQuery(id+"F2.imprint","IMPRINT",EDGE,{"derivedFrom":subQ5}),1.0]])]});}
            var Q39;
            {var subQ0=sQuery(id+"F2.wireOp",EDGE,"E506");Q39=makeQuery(id+"F2.imprint","IMPRINT",FACE,{"disambiguationData":[TD([[makeQuery(id+"F2.imprint","IMPRINT",EDGE,{"derivedFrom":subQ0}),1.0]])]});}
            var Q40;
            {var subQ0=sQuery(id+"F2.wireOp",EDGE,"E561.MirrorCS");Q40=makeQuery(id+"F2.imprint","IMPRINT",FACE,{"disambiguationData":[TD([[makeQuery(id+"F2.imprint","IMPRINT",EDGE,{"derivedFrom":subQ0}),-1.0]])]});}
            var Q41;
            Q41 = qConstructionFilter(qBodyType(qCreatedBy(id + "F2" ,EDGE), BodyType.WIRE), ConstructionObject.NO);
            extrude(context, id + "F3", {"entities" : qUnion([Q0, Q1, Q2, Q3, Q4, Q5, Q6, Q7, Q8, Q9, Q10, Q11, Q12, Q13, Q14, Q15, Q16, Q17, Q18, Q19, Q20, Q21, Q22, Q23, Q24, Q25, Q26, Q27, Q28, Q29, Q30, Q31, Q32, Q33, Q34, Q35, Q36, Q37, Q38, Q39, Q40]), "surfaceEntities" : qUnion([Q41]), "depth" : 6.35 * mm});
        }
    });
